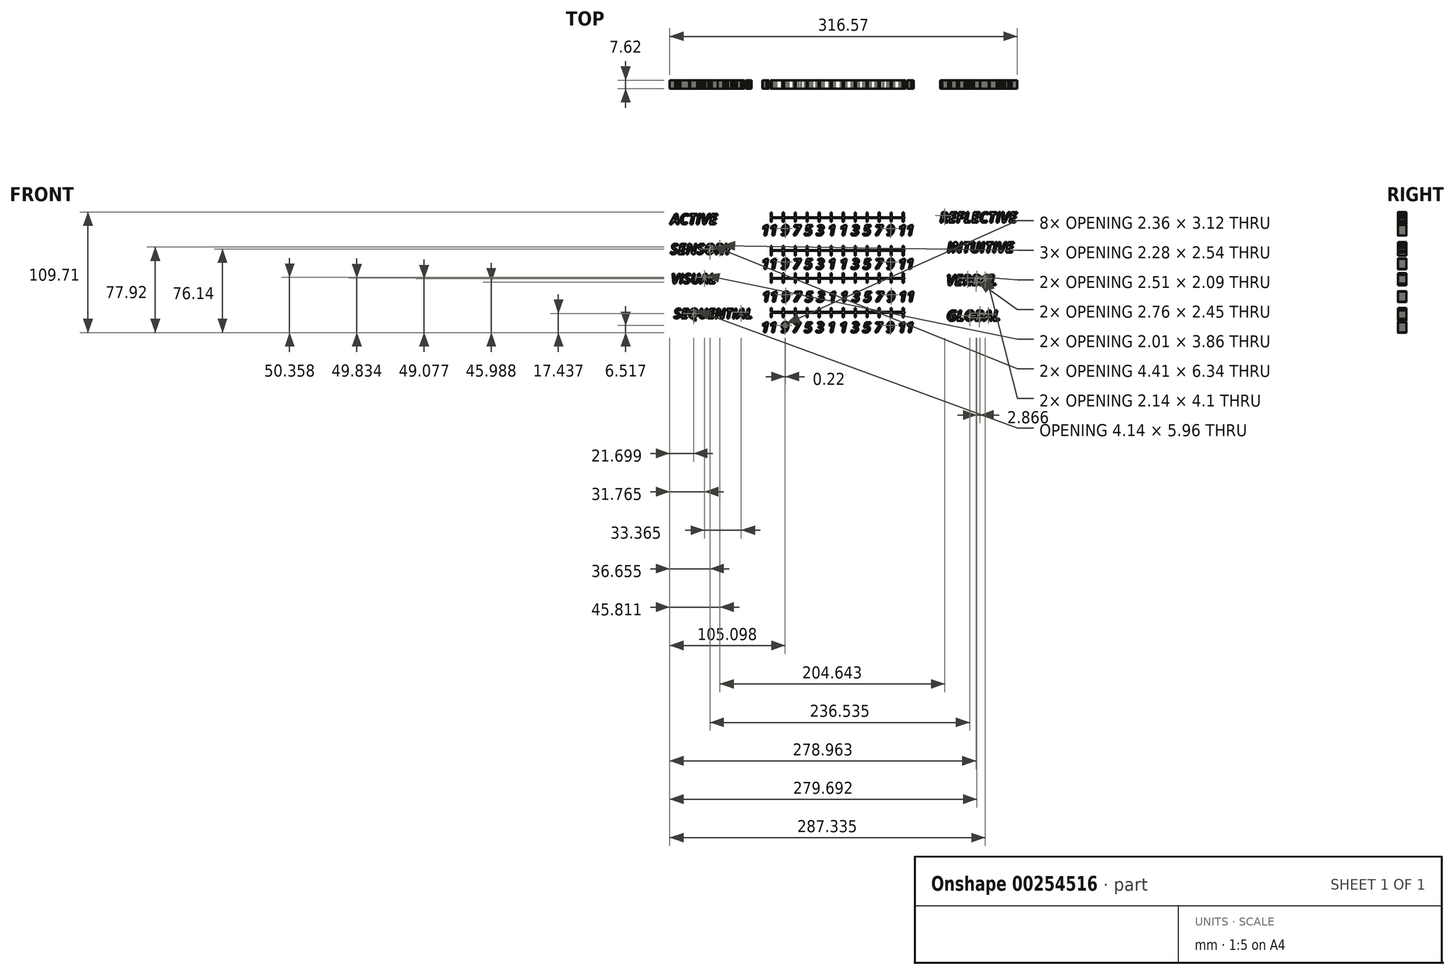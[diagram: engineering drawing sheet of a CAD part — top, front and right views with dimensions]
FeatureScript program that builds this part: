
annotation { "Feature Type Name" : "Feature", "Feature Type Description" : "" }
export const myFeature = defineFeature(function(context is Context, id is Id, definition is map)
    precondition{}
    {
        {
            var Q0;
            Q0=qCreatedBy(makeId("Front.planeOp"),FACE);
            var sketch = newSketch(context, id + "F0", { "sketchPlane" : qUnion([Q0])});
            skText(sketch, "E0", { "text": "ACTIVE", "fontName": "OpenSans-BoldItalic.ttf"});
            skText(sketch, "E1", { "text": "SENSORY", "fontName": "OpenSans-BoldItalic.ttf"});
            skText(sketch, "E2", { "text": "VISUAL", "fontName": "OpenSans-BoldItalic.ttf"});
            skText(sketch, "E3", { "text": "SEQUENTIAL", "fontName": "OpenSans-BoldItalic.ttf"});
            skLineSegment(sketch, "E4", {"start": v(-9.15, 18.36) * mm, "end": v(-99.83, 18.36) * mm});
            skLineSegment(sketch, "E5", {"start": v(-7.58, -9.3) * mm, "end": v(-99.57, -9.3) * mm});
            skLineSegment(sketch, "E6", {"start": v(-99.47, -37.51) * mm, "end": v(-5.07, -37.51) * mm});
            const initialGuessF0  = {"E0": [-0.0995, 0.02725, 1, 0, 0.00948], "E1": [-0.09962, 0, 1, 0, 0.00947], "E2": [-0.09887, -0.02667, 1, 0, 0.0089], "E3": [-0.09653, -0.05842, 1, 0, 0.0089]};
            skSetInitialGuess(sketch, initialGuessF0);
            skSolve(sketch);
        }
        {
            var Q0;
            Q0 = qSketchRegion(id + "F0", true);
            var Q1;
            Q1=qNothing();
            extrude(context, id + "F1", {"entities" : qUnion([Q0, Q1]), "depth" : 7.62 * mm});
        }
        {
            var Q0;
            Q0=qCreatedBy(makeId("Front.planeOp"),FACE);
            var sketch = newSketch(context, id + "F2", { "sketchPlane" : qUnion([Q0])});
            skLineSegment(sketch, "E7.bottom", {"start": v(-101.92, -70.16) * mm, "end": v(120.46, -70.16) * mm});
            skLineSegment(sketch, "E7.top", {"start": v(-101.92, 55.6) * mm, "end": v(120.46, 55.6) * mm});
            skLineSegment(sketch, "E7.left", {"start": v(-101.92, -70.16) * mm, "end": v(-101.92, 55.6) * mm});
            skLineSegment(sketch, "E7.right", {"start": v(120.46, -70.16) * mm, "end": v(120.46, 55.6) * mm});
            skLineSegment(sketch, "E8.bottom", {"start": v(-8.33, 38) * mm, "end": v(-7.22, 38) * mm});
            skLineSegment(sketch, "E8.top", {"start": v(-8.33, 29.27) * mm, "end": v(-7.22, 29.27) * mm});
            skLineSegment(sketch, "E8.left", {"start": v(-8.33, 38) * mm, "end": v(-8.33, 29.27) * mm});
            skLineSegment(sketch, "E8.right", {"start": v(-7.22, 38) * mm, "end": v(-7.22, 29.27) * mm});
            skLineSegment(sketch, "E9.bottom", {"start": v(-8.33, 33.64) * mm, "end": v(113.67, 33.64) * mm});
            skLineSegment(sketch, "E9.top", {"start": v(-8.33, 32.93) * mm, "end": v(113.67, 32.93) * mm});
            skLineSegment(sketch, "E9.left", {"start": v(-8.33, 33.64) * mm, "end": v(-8.33, 32.93) * mm});
            skLineSegment(sketch, "E9.right", {"start": v(113.67, 33.64) * mm, "end": v(113.67, 32.93) * mm});
            skLineSegment(sketch, "E10.1.0.0", {"start": v(2.59, 38) * mm, "end": v(2.59, 29.27) * mm});
            skLineSegment(sketch, "E10.1.0.1", {"start": v(3.7, 38) * mm, "end": v(3.7, 29.27) * mm});
            skLineSegment(sketch, "E10.1.0.2", {"start": v(2.59, 38) * mm, "end": v(3.7, 38) * mm});
            skLineSegment(sketch, "E10.1.0.3", {"start": v(2.59, 29.27) * mm, "end": v(3.7, 29.27) * mm});
            skLineSegment(sketch, "E10.2.0.0", {"start": v(13.51, 38) * mm, "end": v(13.51, 29.27) * mm});
            skLineSegment(sketch, "E10.2.0.1", {"start": v(14.63, 38) * mm, "end": v(14.63, 29.27) * mm});
            skLineSegment(sketch, "E10.2.0.2", {"start": v(13.51, 38) * mm, "end": v(14.63, 38) * mm});
            skLineSegment(sketch, "E10.2.0.3", {"start": v(13.51, 29.27) * mm, "end": v(14.63, 29.27) * mm});
            skLineSegment(sketch, "E10.3.0.0", {"start": v(24.43, 38) * mm, "end": v(24.43, 29.27) * mm});
            skLineSegment(sketch, "E10.3.0.1", {"start": v(25.55, 38) * mm, "end": v(25.55, 29.27) * mm});
            skLineSegment(sketch, "E10.3.0.2", {"start": v(24.43, 38) * mm, "end": v(25.55, 38) * mm});
            skLineSegment(sketch, "E10.3.0.3", {"start": v(24.43, 29.27) * mm, "end": v(25.55, 29.27) * mm});
            skLineSegment(sketch, "E10.4.0.0", {"start": v(35.36, 38) * mm, "end": v(35.36, 29.27) * mm});
            skLineSegment(sketch, "E10.4.0.1", {"start": v(36.47, 38) * mm, "end": v(36.47, 29.27) * mm});
            skLineSegment(sketch, "E10.4.0.2", {"start": v(35.36, 38) * mm, "end": v(36.47, 38) * mm});
            skLineSegment(sketch, "E10.4.0.3", {"start": v(35.36, 29.27) * mm, "end": v(36.47, 29.27) * mm});
            skLineSegment(sketch, "E10.5.0.0", {"start": v(46.28, 38) * mm, "end": v(46.28, 29.27) * mm});
            skLineSegment(sketch, "E10.5.0.1", {"start": v(47.4, 38) * mm, "end": v(47.4, 29.27) * mm});
            skLineSegment(sketch, "E10.5.0.2", {"start": v(46.28, 38) * mm, "end": v(47.4, 38) * mm});
            skLineSegment(sketch, "E10.5.0.3", {"start": v(46.28, 29.27) * mm, "end": v(47.4, 29.27) * mm});
            skLineSegment(sketch, "E10.6.0.0", {"start": v(57.2, 38) * mm, "end": v(57.2, 29.27) * mm});
            skLineSegment(sketch, "E10.6.0.1", {"start": v(58.31, 38) * mm, "end": v(58.31, 29.27) * mm});
            skLineSegment(sketch, "E10.6.0.2", {"start": v(57.2, 38) * mm, "end": v(58.31, 38) * mm});
            skLineSegment(sketch, "E10.6.0.3", {"start": v(57.2, 29.27) * mm, "end": v(58.31, 29.27) * mm});
            skLineSegment(sketch, "E10.7.0.0", {"start": v(68.12, 38) * mm, "end": v(68.12, 29.27) * mm});
            skLineSegment(sketch, "E10.7.0.1", {"start": v(69.24, 38) * mm, "end": v(69.24, 29.27) * mm});
            skLineSegment(sketch, "E10.7.0.2", {"start": v(68.12, 38) * mm, "end": v(69.24, 38) * mm});
            skLineSegment(sketch, "E10.7.0.3", {"start": v(68.12, 29.27) * mm, "end": v(69.24, 29.27) * mm});
            skLineSegment(sketch, "E10.8.0.0", {"start": v(79.04, 38) * mm, "end": v(79.04, 29.27) * mm});
            skLineSegment(sketch, "E10.8.0.1", {"start": v(80.16, 38) * mm, "end": v(80.16, 29.27) * mm});
            skLineSegment(sketch, "E10.8.0.2", {"start": v(79.04, 38) * mm, "end": v(80.16, 38) * mm});
            skLineSegment(sketch, "E10.8.0.3", {"start": v(79.04, 29.27) * mm, "end": v(80.16, 29.27) * mm});
            skLineSegment(sketch, "E10.9.0.0", {"start": v(89.97, 38) * mm, "end": v(89.97, 29.27) * mm});
            skLineSegment(sketch, "E10.9.0.1", {"start": v(91.08, 38) * mm, "end": v(91.08, 29.27) * mm});
            skLineSegment(sketch, "E10.9.0.2", {"start": v(89.97, 38) * mm, "end": v(91.08, 38) * mm});
            skLineSegment(sketch, "E10.9.0.3", {"start": v(89.97, 29.27) * mm, "end": v(91.08, 29.27) * mm});
            skLineSegment(sketch, "E10.10.0.0", {"start": v(100.89, 38) * mm, "end": v(100.89, 29.27) * mm});
            skLineSegment(sketch, "E10.10.0.1", {"start": v(102, 38) * mm, "end": v(102, 29.27) * mm});
            skLineSegment(sketch, "E10.10.0.2", {"start": v(100.89, 38) * mm, "end": v(102, 38) * mm});
            skLineSegment(sketch, "E10.10.0.3", {"start": v(100.89, 29.27) * mm, "end": v(102, 29.27) * mm});
            skLineSegment(sketch, "E10.11.0.0", {"start": v(111.8, 38) * mm, "end": v(111.8, 29.27) * mm});
            skLineSegment(sketch, "E10.11.0.1", {"start": v(112.92, 38) * mm, "end": v(112.92, 29.27) * mm});
            skLineSegment(sketch, "E10.11.0.2", {"start": v(111.8, 38) * mm, "end": v(112.92, 38) * mm});
            skLineSegment(sketch, "E10.11.0.3", {"start": v(111.8, 29.27) * mm, "end": v(112.92, 29.27) * mm});
            skLineSegment(sketch, "E10.direction1", {"start": v(-8.33, 29.27) * mm, "end": v(2.59, 29.27) * mm, "construction": true});
            skLineSegment(sketch, "E11.MirrorCS", {"start": v(2.59, 7.46) * mm, "end": v(3.7, 7.46) * mm});
            skLineSegment(sketch, "E12.MirrorCS", {"start": v(-8.33, 7.46) * mm, "end": v(-7.22, 7.46) * mm});
            skLineSegment(sketch, "E13.MirrorCS", {"start": v(113.67, 3.09) * mm, "end": v(113.67, 3.8) * mm});
            skLineSegment(sketch, "E14.MirrorCS", {"start": v(79.04, 7.46) * mm, "end": v(80.16, 7.46) * mm});
            skLineSegment(sketch, "E15.MirrorCS", {"start": v(111.8, -1.28) * mm, "end": v(112.92, -1.28) * mm});
            skLineSegment(sketch, "E16.MirrorCS", {"start": v(79.04, -1.28) * mm, "end": v(80.16, -1.28) * mm});
            skLineSegment(sketch, "E17.MirrorCS", {"start": v(-8.33, -1.28) * mm, "end": v(-7.22, -1.28) * mm});
            skLineSegment(sketch, "E18.MirrorCS", {"start": v(35.36, 7.46) * mm, "end": v(36.47, 7.46) * mm});
            skLineSegment(sketch, "E19.MirrorCS", {"start": v(13.51, 7.46) * mm, "end": v(14.63, 7.46) * mm});
            skLineSegment(sketch, "E20.MirrorCS", {"start": v(100.89, 7.46) * mm, "end": v(102, 7.46) * mm});
            skLineSegment(sketch, "E21.MirrorCS", {"start": v(-7.22, -1.28) * mm, "end": v(-7.22, 7.46) * mm});
            skLineSegment(sketch, "E22.MirrorCS", {"start": v(24.43, -1.28) * mm, "end": v(25.55, -1.28) * mm});
            skLineSegment(sketch, "E23.MirrorCS", {"start": v(35.36, -1.28) * mm, "end": v(36.47, -1.28) * mm});
            skLineSegment(sketch, "E24.MirrorCS", {"start": v(2.59, -1.28) * mm, "end": v(3.7, -1.28) * mm});
            skLineSegment(sketch, "E25.MirrorCS", {"start": v(111.8, 7.46) * mm, "end": v(112.92, 7.46) * mm});
            skLineSegment(sketch, "E26.MirrorCS", {"start": v(24.43, 7.46) * mm, "end": v(25.55, 7.46) * mm});
            skLineSegment(sketch, "E27.MirrorCS", {"start": v(112.92, -1.28) * mm, "end": v(112.92, 7.46) * mm});
            skLineSegment(sketch, "E28.MirrorCS", {"start": v(89.97, -1.28) * mm, "end": v(91.08, -1.28) * mm});
            skLineSegment(sketch, "E29.MirrorCS", {"start": v(-8.33, 3.09) * mm, "end": v(-8.33, 3.8) * mm});
            skLineSegment(sketch, "E30.MirrorCS", {"start": v(13.51, -1.28) * mm, "end": v(14.63, -1.28) * mm});
            skLineSegment(sketch, "E31.MirrorCS", {"start": v(89.97, 7.46) * mm, "end": v(91.08, 7.46) * mm});
            skLineSegment(sketch, "E32.MirrorCS", {"start": v(68.12, -1.28) * mm, "end": v(69.24, -1.28) * mm});
            skLineSegment(sketch, "E33.MirrorCS", {"start": v(57.2, 7.46) * mm, "end": v(58.31, 7.46) * mm});
            skLineSegment(sketch, "E34.MirrorCS", {"start": v(46.28, 7.46) * mm, "end": v(47.4, 7.46) * mm});
            skLineSegment(sketch, "E35.MirrorCS", {"start": v(68.12, 7.46) * mm, "end": v(69.24, 7.46) * mm});
            skLineSegment(sketch, "E36.MirrorCS", {"start": v(-8.33, -1.28) * mm, "end": v(-8.33, 7.46) * mm});
            skLineSegment(sketch, "E37.MirrorCS", {"start": v(100.89, -1.28) * mm, "end": v(102, -1.28) * mm});
            skLineSegment(sketch, "E38.MirrorCS", {"start": v(111.8, -1.28) * mm, "end": v(111.8, 7.46) * mm});
            skLineSegment(sketch, "E39.MirrorCS", {"start": v(57.2, -1.28) * mm, "end": v(58.31, -1.28) * mm});
            skLineSegment(sketch, "E40.MirrorCS", {"start": v(46.28, -1.28) * mm, "end": v(47.4, -1.28) * mm});
            skLineSegment(sketch, "E41.MirrorCS", {"start": v(-8.33, 3.09) * mm, "end": v(113.67, 3.09) * mm});
            skLineSegment(sketch, "E42.MirrorCS", {"start": v(36.47, -1.28) * mm, "end": v(36.47, 7.46) * mm});
            skLineSegment(sketch, "E43.MirrorCS", {"start": v(35.36, -1.28) * mm, "end": v(35.36, 7.46) * mm});
            skLineSegment(sketch, "E44.MirrorCS", {"start": v(13.51, -1.28) * mm, "end": v(13.51, 7.46) * mm});
            skLineSegment(sketch, "E45.MirrorCS", {"start": v(80.16, -1.28) * mm, "end": v(80.16, 7.46) * mm});
            skLineSegment(sketch, "E46.MirrorCS", {"start": v(69.24, -1.28) * mm, "end": v(69.24, 7.46) * mm});
            skLineSegment(sketch, "E47.MirrorCS", {"start": v(14.63, -1.28) * mm, "end": v(14.63, 7.46) * mm});
            skLineSegment(sketch, "E48.MirrorCS", {"start": v(100.89, -1.28) * mm, "end": v(100.89, 7.46) * mm});
            skLineSegment(sketch, "E49.MirrorCS", {"start": v(25.55, -1.28) * mm, "end": v(25.55, 7.46) * mm});
            skLineSegment(sketch, "E50.MirrorCS", {"start": v(-8.33, 3.8) * mm, "end": v(113.67, 3.8) * mm});
            skLineSegment(sketch, "E51.MirrorCS", {"start": v(91.08, -1.28) * mm, "end": v(91.08, 7.46) * mm});
            skLineSegment(sketch, "E52.MirrorCS", {"start": v(102, -1.28) * mm, "end": v(102, 7.46) * mm});
            skLineSegment(sketch, "E53.MirrorCS", {"start": v(57.2, -1.28) * mm, "end": v(57.2, 7.46) * mm});
            skLineSegment(sketch, "E54.MirrorCS", {"start": v(89.97, -1.28) * mm, "end": v(89.97, 7.46) * mm});
            skLineSegment(sketch, "E55.MirrorCS", {"start": v(-8.33, 7.46) * mm, "end": v(2.59, 7.46) * mm, "construction": true});
            skLineSegment(sketch, "E56.MirrorCS", {"start": v(47.4, -1.28) * mm, "end": v(47.4, 7.46) * mm});
            skLineSegment(sketch, "E57.MirrorCS", {"start": v(68.12, -1.28) * mm, "end": v(68.12, 7.46) * mm});
            skLineSegment(sketch, "E58.MirrorCS", {"start": v(2.59, -1.28) * mm, "end": v(2.59, 7.46) * mm});
            skLineSegment(sketch, "E59.MirrorCS", {"start": v(24.43, -1.28) * mm, "end": v(24.43, 7.46) * mm});
            skLineSegment(sketch, "E60.MirrorCS", {"start": v(3.7, -1.28) * mm, "end": v(3.7, 7.46) * mm});
            skLineSegment(sketch, "E61.MirrorCS", {"start": v(79.04, -1.28) * mm, "end": v(79.04, 7.46) * mm});
            skLineSegment(sketch, "E62.MirrorCS", {"start": v(46.28, -1.28) * mm, "end": v(46.28, 7.46) * mm});
            skLineSegment(sketch, "E63.MirrorCS", {"start": v(58.31, -1.28) * mm, "end": v(58.31, 7.46) * mm});
            skLineSegment(sketch, "E64.MirrorCS", {"start": v(-8.33, -26.06) * mm, "end": v(-7.22, -26.06) * mm});
            skLineSegment(sketch, "E65.MirrorCS", {"start": v(2.59, -26.06) * mm, "end": v(3.7, -26.06) * mm});
            skLineSegment(sketch, "E66.MirrorCS", {"start": v(79.04, -17.33) * mm, "end": v(80.16, -17.33) * mm});
            skLineSegment(sketch, "E67.MirrorCS", {"start": v(-8.33, -17.33) * mm, "end": v(-7.22, -17.33) * mm});
            skLineSegment(sketch, "E68.MirrorCS", {"start": v(57.2, -26.06) * mm, "end": v(58.31, -26.06) * mm});
            skLineSegment(sketch, "E69.MirrorCS", {"start": v(57.2, -17.33) * mm, "end": v(58.31, -17.33) * mm});
            skLineSegment(sketch, "E70.MirrorCS", {"start": v(46.28, -26.06) * mm, "end": v(47.4, -26.06) * mm});
            skLineSegment(sketch, "E71.MirrorCS", {"start": v(35.36, -26.06) * mm, "end": v(36.47, -26.06) * mm});
            skLineSegment(sketch, "E72.MirrorCS", {"start": v(35.36, -17.33) * mm, "end": v(36.47, -17.33) * mm});
            skLineSegment(sketch, "E73.MirrorCS", {"start": v(68.12, -26.06) * mm, "end": v(69.24, -26.06) * mm});
            skLineSegment(sketch, "E74.MirrorCS", {"start": v(13.51, -26.06) * mm, "end": v(14.63, -26.06) * mm});
            skLineSegment(sketch, "E75.MirrorCS", {"start": v(-8.33, -17.33) * mm, "end": v(-8.33, -26.06) * mm});
            skLineSegment(sketch, "E76.MirrorCS", {"start": v(100.89, -26.06) * mm, "end": v(102, -26.06) * mm});
            skLineSegment(sketch, "E77.MirrorCS", {"start": v(46.28, -17.33) * mm, "end": v(47.4, -17.33) * mm});
            skLineSegment(sketch, "E78.MirrorCS", {"start": v(2.59, -17.33) * mm, "end": v(3.7, -17.33) * mm});
            skLineSegment(sketch, "E79.MirrorCS", {"start": v(68.12, -17.33) * mm, "end": v(69.24, -17.33) * mm});
            skLineSegment(sketch, "E80.MirrorCS", {"start": v(13.51, -17.33) * mm, "end": v(14.63, -17.33) * mm});
            skLineSegment(sketch, "E81.MirrorCS", {"start": v(79.04, -26.06) * mm, "end": v(80.16, -26.06) * mm});
            skLineSegment(sketch, "E82.MirrorCS", {"start": v(111.8, -17.33) * mm, "end": v(112.92, -17.33) * mm});
            skLineSegment(sketch, "E83.MirrorCS", {"start": v(89.97, -26.06) * mm, "end": v(91.08, -26.06) * mm});
            skLineSegment(sketch, "E84.MirrorCS", {"start": v(-8.33, -21.7) * mm, "end": v(-8.33, -22.4) * mm});
            skLineSegment(sketch, "E85.MirrorCS", {"start": v(113.67, -21.7) * mm, "end": v(113.67, -22.4) * mm});
            skLineSegment(sketch, "E86.MirrorCS", {"start": v(24.43, -26.06) * mm, "end": v(25.55, -26.06) * mm});
            skLineSegment(sketch, "E87.MirrorCS", {"start": v(24.43, -17.33) * mm, "end": v(25.55, -17.33) * mm});
            skLineSegment(sketch, "E88.MirrorCS", {"start": v(-7.22, -17.33) * mm, "end": v(-7.22, -26.06) * mm});
            skLineSegment(sketch, "E89.MirrorCS", {"start": v(111.8, -17.33) * mm, "end": v(111.8, -26.06) * mm});
            skLineSegment(sketch, "E90.MirrorCS", {"start": v(111.8, -26.06) * mm, "end": v(112.92, -26.06) * mm});
            skLineSegment(sketch, "E91.MirrorCS", {"start": v(112.92, -17.33) * mm, "end": v(112.92, -26.06) * mm});
            skLineSegment(sketch, "E92.MirrorCS", {"start": v(89.97, -17.33) * mm, "end": v(91.08, -17.33) * mm});
            skLineSegment(sketch, "E93.MirrorCS", {"start": v(100.89, -17.33) * mm, "end": v(102, -17.33) * mm});
            skLineSegment(sketch, "E94.MirrorCS", {"start": v(100.89, -17.33) * mm, "end": v(100.89, -26.06) * mm});
            skLineSegment(sketch, "E95.MirrorCS", {"start": v(25.55, -17.33) * mm, "end": v(25.55, -26.06) * mm});
            skLineSegment(sketch, "E96.MirrorCS", {"start": v(-8.33, -26.06) * mm, "end": v(2.59, -26.06) * mm, "construction": true});
            skLineSegment(sketch, "E97.MirrorCS", {"start": v(-8.33, -22.4) * mm, "end": v(113.67, -22.4) * mm});
            skLineSegment(sketch, "E98.MirrorCS", {"start": v(91.08, -17.33) * mm, "end": v(91.08, -26.06) * mm});
            skLineSegment(sketch, "E99.MirrorCS", {"start": v(102, -17.33) * mm, "end": v(102, -26.06) * mm});
            skLineSegment(sketch, "E100.MirrorCS", {"start": v(47.4, -17.33) * mm, "end": v(47.4, -26.06) * mm});
            skLineSegment(sketch, "E101.MirrorCS", {"start": v(69.24, -17.33) * mm, "end": v(69.24, -26.06) * mm});
            skLineSegment(sketch, "E102.MirrorCS", {"start": v(46.28, -17.33) * mm, "end": v(46.28, -26.06) * mm});
            skLineSegment(sketch, "E103.MirrorCS", {"start": v(58.31, -17.33) * mm, "end": v(58.31, -26.06) * mm});
            skLineSegment(sketch, "E104.MirrorCS", {"start": v(14.63, -17.33) * mm, "end": v(14.63, -26.06) * mm});
            skLineSegment(sketch, "E105.MirrorCS", {"start": v(80.16, -17.33) * mm, "end": v(80.16, -26.06) * mm});
            skLineSegment(sketch, "E106.MirrorCS", {"start": v(79.04, -17.33) * mm, "end": v(79.04, -26.06) * mm});
            skLineSegment(sketch, "E107.MirrorCS", {"start": v(68.12, -17.33) * mm, "end": v(68.12, -26.06) * mm});
            skLineSegment(sketch, "E108.MirrorCS", {"start": v(24.43, -17.33) * mm, "end": v(24.43, -26.06) * mm});
            skLineSegment(sketch, "E109.MirrorCS", {"start": v(89.97, -17.33) * mm, "end": v(89.97, -26.06) * mm});
            skLineSegment(sketch, "E110.MirrorCS", {"start": v(13.51, -17.33) * mm, "end": v(13.51, -26.06) * mm});
            skLineSegment(sketch, "E111.MirrorCS", {"start": v(-8.33, -21.7) * mm, "end": v(113.67, -21.7) * mm});
            skLineSegment(sketch, "E112.MirrorCS", {"start": v(2.59, -17.33) * mm, "end": v(2.59, -26.06) * mm});
            skLineSegment(sketch, "E113.MirrorCS", {"start": v(3.7, -17.33) * mm, "end": v(3.7, -26.06) * mm});
            skLineSegment(sketch, "E114.MirrorCS", {"start": v(35.36, -17.33) * mm, "end": v(35.36, -26.06) * mm});
            skLineSegment(sketch, "E115.MirrorCS", {"start": v(36.47, -17.33) * mm, "end": v(36.47, -26.06) * mm});
            skLineSegment(sketch, "E116.MirrorCS", {"start": v(57.2, -17.33) * mm, "end": v(57.2, -26.06) * mm});
            skLineSegment(sketch, "E117.MirrorCS", {"start": v(2.59, -48.96) * mm, "end": v(3.7, -48.96) * mm});
            skLineSegment(sketch, "E118.MirrorCS", {"start": v(-8.33, -53.33) * mm, "end": v(-8.33, -52.62) * mm});
            skLineSegment(sketch, "E119.MirrorCS", {"start": v(-8.33, -48.96) * mm, "end": v(-7.22, -48.96) * mm});
            skLineSegment(sketch, "E120.MirrorCS", {"start": v(89.97, -48.96) * mm, "end": v(91.08, -48.96) * mm});
            skLineSegment(sketch, "E121.MirrorCS", {"start": v(89.97, -57.7) * mm, "end": v(91.08, -57.7) * mm});
            skLineSegment(sketch, "E122.MirrorCS", {"start": v(100.89, -48.96) * mm, "end": v(102, -48.96) * mm});
            skLineSegment(sketch, "E123.MirrorCS", {"start": v(112.92, -57.7) * mm, "end": v(112.92, -48.96) * mm});
            skLineSegment(sketch, "E124.MirrorCS", {"start": v(-8.33, -57.7) * mm, "end": v(-8.33, -48.96) * mm});
            skLineSegment(sketch, "E125.MirrorCS", {"start": v(111.8, -48.96) * mm, "end": v(112.92, -48.96) * mm});
            skLineSegment(sketch, "E126.MirrorCS", {"start": v(13.51, -48.96) * mm, "end": v(14.63, -48.96) * mm});
            skLineSegment(sketch, "E127.MirrorCS", {"start": v(79.04, -57.7) * mm, "end": v(80.16, -57.7) * mm});
            skLineSegment(sketch, "E128.MirrorCS", {"start": v(111.8, -57.7) * mm, "end": v(112.92, -57.7) * mm});
            skLineSegment(sketch, "E129.MirrorCS", {"start": v(68.12, -48.96) * mm, "end": v(69.24, -48.96) * mm});
            skLineSegment(sketch, "E130.MirrorCS", {"start": v(79.04, -48.96) * mm, "end": v(80.16, -48.96) * mm});
            skLineSegment(sketch, "E131.MirrorCS", {"start": v(35.36, -57.7) * mm, "end": v(36.47, -57.7) * mm});
            skLineSegment(sketch, "E132.MirrorCS", {"start": v(-7.22, -57.7) * mm, "end": v(-7.22, -48.96) * mm});
            skLineSegment(sketch, "E133.MirrorCS", {"start": v(46.28, -48.96) * mm, "end": v(47.4, -48.96) * mm});
            skLineSegment(sketch, "E134.MirrorCS", {"start": v(24.43, -48.96) * mm, "end": v(25.55, -48.96) * mm});
            skLineSegment(sketch, "E135.MirrorCS", {"start": v(57.2, -57.7) * mm, "end": v(58.31, -57.7) * mm});
            skLineSegment(sketch, "E136.MirrorCS", {"start": v(113.67, -53.33) * mm, "end": v(113.67, -52.62) * mm});
            skLineSegment(sketch, "E137.MirrorCS", {"start": v(46.28, -57.7) * mm, "end": v(47.4, -57.7) * mm});
            skLineSegment(sketch, "E138.MirrorCS", {"start": v(100.89, -57.7) * mm, "end": v(102, -57.7) * mm});
            skLineSegment(sketch, "E139.MirrorCS", {"start": v(68.12, -57.7) * mm, "end": v(69.24, -57.7) * mm});
            skLineSegment(sketch, "E140.MirrorCS", {"start": v(-8.33, -57.7) * mm, "end": v(-7.22, -57.7) * mm});
            skLineSegment(sketch, "E141.MirrorCS", {"start": v(13.51, -57.7) * mm, "end": v(14.63, -57.7) * mm});
            skLineSegment(sketch, "E142.MirrorCS", {"start": v(57.2, -48.96) * mm, "end": v(58.31, -48.96) * mm});
            skLineSegment(sketch, "E143.MirrorCS", {"start": v(35.36, -48.96) * mm, "end": v(36.47, -48.96) * mm});
            skLineSegment(sketch, "E144.MirrorCS", {"start": v(24.43, -57.7) * mm, "end": v(25.55, -57.7) * mm});
            skLineSegment(sketch, "E145.MirrorCS", {"start": v(2.59, -57.7) * mm, "end": v(3.7, -57.7) * mm});
            skLineSegment(sketch, "E146.MirrorCS", {"start": v(102, -57.7) * mm, "end": v(102, -48.96) * mm});
            skLineSegment(sketch, "E147.MirrorCS", {"start": v(24.43, -57.7) * mm, "end": v(24.43, -48.96) * mm});
            skLineSegment(sketch, "E148.MirrorCS", {"start": v(68.12, -57.7) * mm, "end": v(68.12, -48.96) * mm});
            skLineSegment(sketch, "E149.MirrorCS", {"start": v(79.04, -57.7) * mm, "end": v(79.04, -48.96) * mm});
            skLineSegment(sketch, "E150.MirrorCS", {"start": v(35.36, -57.7) * mm, "end": v(35.36, -48.96) * mm});
            skLineSegment(sketch, "E151.MirrorCS", {"start": v(91.08, -57.7) * mm, "end": v(91.08, -48.96) * mm});
            skLineSegment(sketch, "E152.MirrorCS", {"start": v(111.8, -57.7) * mm, "end": v(111.8, -48.96) * mm});
            skLineSegment(sketch, "E153.MirrorCS", {"start": v(80.16, -57.7) * mm, "end": v(80.16, -48.96) * mm});
            skLineSegment(sketch, "E154.MirrorCS", {"start": v(3.7, -57.7) * mm, "end": v(3.7, -48.96) * mm});
            skLineSegment(sketch, "E155.MirrorCS", {"start": v(14.63, -57.7) * mm, "end": v(14.63, -48.96) * mm});
            skLineSegment(sketch, "E156.MirrorCS", {"start": v(-8.33, -52.62) * mm, "end": v(113.67, -52.62) * mm});
            skLineSegment(sketch, "E157.MirrorCS", {"start": v(46.28, -57.7) * mm, "end": v(46.28, -48.96) * mm});
            skLineSegment(sketch, "E158.MirrorCS", {"start": v(69.24, -57.7) * mm, "end": v(69.24, -48.96) * mm});
            skLineSegment(sketch, "E159.MirrorCS", {"start": v(89.97, -57.7) * mm, "end": v(89.97, -48.96) * mm});
            skLineSegment(sketch, "E160.MirrorCS", {"start": v(25.55, -57.7) * mm, "end": v(25.55, -48.96) * mm});
            skLineSegment(sketch, "E161.MirrorCS", {"start": v(-8.33, -53.33) * mm, "end": v(113.67, -53.33) * mm});
            skLineSegment(sketch, "E162.MirrorCS", {"start": v(13.51, -57.7) * mm, "end": v(13.51, -48.96) * mm});
            skLineSegment(sketch, "E163.MirrorCS", {"start": v(58.31, -57.7) * mm, "end": v(58.31, -48.96) * mm});
            skLineSegment(sketch, "E164.MirrorCS", {"start": v(36.47, -57.7) * mm, "end": v(36.47, -48.96) * mm});
            skLineSegment(sketch, "E165.MirrorCS", {"start": v(57.2, -57.7) * mm, "end": v(57.2, -48.96) * mm});
            skLineSegment(sketch, "E166.MirrorCS", {"start": v(2.59, -57.7) * mm, "end": v(2.59, -48.96) * mm});
            skLineSegment(sketch, "E167.MirrorCS", {"start": v(100.89, -57.7) * mm, "end": v(100.89, -48.96) * mm});
            skLineSegment(sketch, "E168.MirrorCS", {"start": v(47.4, -57.7) * mm, "end": v(47.4, -48.96) * mm});
            skLineSegment(sketch, "E169.MirrorCS", {"start": v(-8.33, -48.96) * mm, "end": v(2.59, -48.96) * mm, "construction": true});
            skSolve(sketch);
        }
        {
            var Q0;
            {var subQ0=sQuery(id+"F2.wireOp",EDGE,"E126.MirrorCS");Q0=makeQuery(id+"F2.imprint","IMPRINT",FACE,{"disambiguationData":[TD([[makeQuery(id+"F2.imprint","IMPRINT",EDGE,{"derivedFrom":subQ0}),-1.0]])]});}
            var Q1;
            {var subQ0=sQuery(id+"F2.wireOp",EDGE,"E142.MirrorCS");Q1=makeQuery(id+"F2.imprint","IMPRINT",FACE,{"disambiguationData":[TD([[makeQuery(id+"F2.imprint","IMPRINT",EDGE,{"derivedFrom":subQ0}),-1.0]])]});}
            var Q2;
            {var subQ0=sQuery(id+"F2.wireOp",EDGE,"E83.MirrorCS");Q2=makeQuery(id+"F2.imprint","IMPRINT",FACE,{"disambiguationData":[TD([[makeQuery(id+"F2.imprint","IMPRINT",EDGE,{"derivedFrom":subQ0}),1.0]])]});}
            var Q3;
            {var subQ0=sQuery(id+"F2.wireOp",EDGE,"E79.MirrorCS");Q3=makeQuery(id+"F2.imprint","IMPRINT",FACE,{"disambiguationData":[TD([[makeQuery(id+"F2.imprint","IMPRINT",EDGE,{"derivedFrom":subQ0}),-1.0]])]});}
            var Q4;
            {var subQ5=sQuery(id+"F2.wireOp",EDGE,"E10.7.0.3");Q4=makeQuery(id+"F2.imprint","IMPRINT",FACE,{"disambiguationData":[TD([[makeQuery(id+"F2.imprint","IMPRINT",EDGE,{"derivedFrom":subQ5}),1.0]])]});}
            var Q5;
            {var subQ0=sQuery(id+"F2.wireOp",EDGE,"E121.MirrorCS");Q5=makeQuery(id+"F2.imprint","IMPRINT",FACE,{"disambiguationData":[TD([[makeQuery(id+"F2.imprint","IMPRINT",EDGE,{"derivedFrom":subQ0}),1.0]])]});}
            var Q6;
            {var subQ5=sQuery(id+"F2.wireOp",EDGE,"E10.6.0.3");Q6=makeQuery(id+"F2.imprint","IMPRINT",FACE,{"disambiguationData":[TD([[makeQuery(id+"F2.imprint","IMPRINT",EDGE,{"derivedFrom":subQ5}),1.0]])]});}
            var Q7;
            {var subQ0=sQuery(id+"F2.wireOp",EDGE,"E19.MirrorCS");Q7=makeQuery(id+"F2.imprint","IMPRINT",FACE,{"disambiguationData":[TD([[makeQuery(id+"F2.imprint","IMPRINT",EDGE,{"derivedFrom":subQ0}),-1.0]])]});}
            var Q8;
            {var subQ0=sQuery(id+"F2.wireOp",EDGE,"E140.MirrorCS");Q8=makeQuery(id+"F2.imprint","IMPRINT",FACE,{"disambiguationData":[TD([[makeQuery(id+"F2.imprint","IMPRINT",EDGE,{"derivedFrom":subQ0}),1.0]])]});}
            var Q9;
            {var subQ0=sQuery(id+"F2.wireOp",EDGE,"E80.MirrorCS");Q9=makeQuery(id+"F2.imprint","IMPRINT",FACE,{"disambiguationData":[TD([[makeQuery(id+"F2.imprint","IMPRINT",EDGE,{"derivedFrom":subQ0}),-1.0]])]});}
            var Q10;
            {var subQ0=sQuery(id+"F2.wireOp",EDGE,"E35.MirrorCS");Q10=makeQuery(id+"F2.imprint","IMPRINT",FACE,{"disambiguationData":[TD([[makeQuery(id+"F2.imprint","IMPRINT",EDGE,{"derivedFrom":subQ0}),-1.0]])]});}
            var Q11;
            {var subQ0=sQuery(id+"F2.wireOp",EDGE,"E39.MirrorCS");Q11=makeQuery(id+"F2.imprint","IMPRINT",FACE,{"disambiguationData":[TD([[makeQuery(id+"F2.imprint","IMPRINT",EDGE,{"derivedFrom":subQ0}),1.0]])]});}
            var Q12;
            {var subQ0=sQuery(id+"F2.wireOp",EDGE,"E22.MirrorCS");Q12=makeQuery(id+"F2.imprint","IMPRINT",FACE,{"disambiguationData":[TD([[makeQuery(id+"F2.imprint","IMPRINT",EDGE,{"derivedFrom":subQ0}),1.0]])]});}
            var Q13;
            {var subQ0=sQuery(id+"F2.wireOp",EDGE,"E139.MirrorCS");Q13=makeQuery(id+"F2.imprint","IMPRINT",FACE,{"disambiguationData":[TD([[makeQuery(id+"F2.imprint","IMPRINT",EDGE,{"derivedFrom":subQ0}),1.0]])]});}
            var Q14;
            {var subQ5=sQuery(id+"F2.wireOp",EDGE,"E10.3.0.3");Q14=makeQuery(id+"F2.imprint","IMPRINT",FACE,{"disambiguationData":[TD([[makeQuery(id+"F2.imprint","IMPRINT",EDGE,{"derivedFrom":subQ5}),1.0]])]});}
            var Q15;
            {var subQ0=sQuery(id+"F2.wireOp",EDGE,"E119.MirrorCS");Q15=makeQuery(id+"F2.imprint","IMPRINT",FACE,{"disambiguationData":[TD([[makeQuery(id+"F2.imprint","IMPRINT",EDGE,{"derivedFrom":subQ0}),-1.0]])]});}
            var Q16;
            {var subQ0=sQuery(id+"F2.wireOp",EDGE,"E33.MirrorCS");Q16=makeQuery(id+"F2.imprint","IMPRINT",FACE,{"disambiguationData":[TD([[makeQuery(id+"F2.imprint","IMPRINT",EDGE,{"derivedFrom":subQ0}),-1.0]])]});}
            var Q17;
            {var subQ0=sQuery(id+"F2.wireOp",EDGE,"E74.MirrorCS");Q17=makeQuery(id+"F2.imprint","IMPRINT",FACE,{"disambiguationData":[TD([[makeQuery(id+"F2.imprint","IMPRINT",EDGE,{"derivedFrom":subQ0}),1.0]])]});}
            var Q18;
            {var subQ0=sQuery(id+"F2.wireOp",EDGE,"E138.MirrorCS");Q18=makeQuery(id+"F2.imprint","IMPRINT",FACE,{"disambiguationData":[TD([[makeQuery(id+"F2.imprint","IMPRINT",EDGE,{"derivedFrom":subQ0}),1.0]])]});}
            var Q19;
            {var subQ0=sQuery(id+"F2.wireOp",EDGE,"E76.MirrorCS");Q19=makeQuery(id+"F2.imprint","IMPRINT",FACE,{"disambiguationData":[TD([[makeQuery(id+"F2.imprint","IMPRINT",EDGE,{"derivedFrom":subQ0}),1.0]])]});}
            var Q20;
            {var subQ0=sQuery(id+"F2.wireOp",EDGE,"E120.MirrorCS");Q20=makeQuery(id+"F2.imprint","IMPRINT",FACE,{"disambiguationData":[TD([[makeQuery(id+"F2.imprint","IMPRINT",EDGE,{"derivedFrom":subQ0}),-1.0]])]});}
            var Q21;
            {var subQ0=sQuery(id+"F2.wireOp",EDGE,"E144.MirrorCS");Q21=makeQuery(id+"F2.imprint","IMPRINT",FACE,{"disambiguationData":[TD([[makeQuery(id+"F2.imprint","IMPRINT",EDGE,{"derivedFrom":subQ0}),1.0]])]});}
            var Q22;
            {var subQ0=sQuery(id+"F2.wireOp",EDGE,"E37.MirrorCS");Q22=makeQuery(id+"F2.imprint","IMPRINT",FACE,{"disambiguationData":[TD([[makeQuery(id+"F2.imprint","IMPRINT",EDGE,{"derivedFrom":subQ0}),1.0]])]});}
            var Q23;
            {var subQ0=sQuery(id+"F2.wireOp",EDGE,"E122.MirrorCS");Q23=makeQuery(id+"F2.imprint","IMPRINT",FACE,{"disambiguationData":[TD([[makeQuery(id+"F2.imprint","IMPRINT",EDGE,{"derivedFrom":subQ0}),-1.0]])]});}
            var Q24;
            {var subQ0=sQuery(id+"F2.wireOp",EDGE,"E141.MirrorCS");Q24=makeQuery(id+"F2.imprint","IMPRINT",FACE,{"disambiguationData":[TD([[makeQuery(id+"F2.imprint","IMPRINT",EDGE,{"derivedFrom":subQ0}),1.0]])]});}
            var Q25;
            {var subQ0=sQuery(id+"F2.wireOp",EDGE,"E17.MirrorCS");Q25=makeQuery(id+"F2.imprint","IMPRINT",FACE,{"disambiguationData":[TD([[makeQuery(id+"F2.imprint","IMPRINT",EDGE,{"derivedFrom":subQ0}),1.0]])]});}
            var Q26;
            {var subQ0=sQuery(id+"F2.wireOp",EDGE,"E20.MirrorCS");Q26=makeQuery(id+"F2.imprint","IMPRINT",FACE,{"disambiguationData":[TD([[makeQuery(id+"F2.imprint","IMPRINT",EDGE,{"derivedFrom":subQ0}),-1.0]])]});}
            var Q27;
            {var subQ0=sQuery(id+"F2.wireOp",EDGE,"E64.MirrorCS");Q27=makeQuery(id+"F2.imprint","IMPRINT",FACE,{"disambiguationData":[TD([[makeQuery(id+"F2.imprint","IMPRINT",EDGE,{"derivedFrom":subQ0}),1.0]])]});}
            var Q28;
            {var subQ0=sQuery(id+"F2.wireOp",EDGE,"E67.MirrorCS");Q28=makeQuery(id+"F2.imprint","IMPRINT",FACE,{"disambiguationData":[TD([[makeQuery(id+"F2.imprint","IMPRINT",EDGE,{"derivedFrom":subQ0}),-1.0]])]});}
            var Q29;
            {var subQ0=sQuery(id+"F2.wireOp",EDGE,"E68.MirrorCS");Q29=makeQuery(id+"F2.imprint","IMPRINT",FACE,{"disambiguationData":[TD([[makeQuery(id+"F2.imprint","IMPRINT",EDGE,{"derivedFrom":subQ0}),1.0]])]});}
            var Q30;
            {var subQ5=sQuery(id+"F2.wireOp",EDGE,"E10.9.0.3");Q30=makeQuery(id+"F2.imprint","IMPRINT",FACE,{"disambiguationData":[TD([[makeQuery(id+"F2.imprint","IMPRINT",EDGE,{"derivedFrom":subQ5}),1.0]])]});}
            var Q31;
            {var subQ0=sQuery(id+"F2.wireOp",EDGE,"E129.MirrorCS");Q31=makeQuery(id+"F2.imprint","IMPRINT",FACE,{"disambiguationData":[TD([[makeQuery(id+"F2.imprint","IMPRINT",EDGE,{"derivedFrom":subQ0}),-1.0]])]});}
            var Q32;
            {var subQ0=sQuery(id+"F2.wireOp",EDGE,"E86.MirrorCS");Q32=makeQuery(id+"F2.imprint","IMPRINT",FACE,{"disambiguationData":[TD([[makeQuery(id+"F2.imprint","IMPRINT",EDGE,{"derivedFrom":subQ0}),1.0]])]});}
            var Q33;
            {var subQ0=sQuery(id+"F2.wireOp",EDGE,"E87.MirrorCS");Q33=makeQuery(id+"F2.imprint","IMPRINT",FACE,{"disambiguationData":[TD([[makeQuery(id+"F2.imprint","IMPRINT",EDGE,{"derivedFrom":subQ0}),-1.0]])]});}
            var Q34;
            {var subQ0=sQuery(id+"F2.wireOp",EDGE,"E69.MirrorCS");Q34=makeQuery(id+"F2.imprint","IMPRINT",FACE,{"disambiguationData":[TD([[makeQuery(id+"F2.imprint","IMPRINT",EDGE,{"derivedFrom":subQ0}),-1.0]])]});}
            var Q35;
            {var subQ0=sQuery(id+"F2.wireOp",EDGE,"E26.MirrorCS");Q35=makeQuery(id+"F2.imprint","IMPRINT",FACE,{"disambiguationData":[TD([[makeQuery(id+"F2.imprint","IMPRINT",EDGE,{"derivedFrom":subQ0}),-1.0]])]});}
            var Q36;
            {var subQ5=sQuery(id+"F2.wireOp",EDGE,"E10.10.0.3");Q36=makeQuery(id+"F2.imprint","IMPRINT",FACE,{"disambiguationData":[TD([[makeQuery(id+"F2.imprint","IMPRINT",EDGE,{"derivedFrom":subQ5}),1.0]])]});}
            var Q37;
            {var subQ0=sQuery(id+"F2.wireOp",EDGE,"E28.MirrorCS");Q37=makeQuery(id+"F2.imprint","IMPRINT",FACE,{"disambiguationData":[TD([[makeQuery(id+"F2.imprint","IMPRINT",EDGE,{"derivedFrom":subQ0}),1.0]])]});}
            var Q38;
            {var subQ0=sQuery(id+"F2.wireOp",EDGE,"E30.MirrorCS");Q38=makeQuery(id+"F2.imprint","IMPRINT",FACE,{"disambiguationData":[TD([[makeQuery(id+"F2.imprint","IMPRINT",EDGE,{"derivedFrom":subQ0}),1.0]])]});}
            var Q39;
            {var subQ0=sQuery(id+"F2.wireOp",EDGE,"E92.MirrorCS");Q39=makeQuery(id+"F2.imprint","IMPRINT",FACE,{"disambiguationData":[TD([[makeQuery(id+"F2.imprint","IMPRINT",EDGE,{"derivedFrom":subQ0}),-1.0]])]});}
            var Q40;
            {var subQ5=sQuery(id+"F2.wireOp",EDGE,"E10.2.0.3");Q40=makeQuery(id+"F2.imprint","IMPRINT",FACE,{"disambiguationData":[TD([[makeQuery(id+"F2.imprint","IMPRINT",EDGE,{"derivedFrom":subQ5}),1.0]])]});}
            var Q41;
            {var subQ0=sQuery(id+"F2.wireOp",EDGE,"E8.bottom");Q41=makeQuery(id+"F2.imprint","IMPRINT",FACE,{"disambiguationData":[TD([[makeQuery(id+"F2.imprint","IMPRINT",EDGE,{"derivedFrom":subQ0}),-1.0]])]});}
            var Q42;
            {var subQ0=sQuery(id+"F2.wireOp",EDGE,"E8.top");Q42=makeQuery(id+"F2.imprint","IMPRINT",FACE,{"disambiguationData":[TD([[makeQuery(id+"F2.imprint","IMPRINT",EDGE,{"derivedFrom":subQ0}),1.0]])]});}
            var Q43;
            {var subQ5=sQuery(id+"F2.wireOp",EDGE,"E10.2.0.2");Q43=makeQuery(id+"F2.imprint","IMPRINT",FACE,{"disambiguationData":[TD([[makeQuery(id+"F2.imprint","IMPRINT",EDGE,{"derivedFrom":subQ5}),-1.0]])]});}
            var Q44;
            {var subQ5=sQuery(id+"F2.wireOp",EDGE,"E10.3.0.2");Q44=makeQuery(id+"F2.imprint","IMPRINT",FACE,{"disambiguationData":[TD([[makeQuery(id+"F2.imprint","IMPRINT",EDGE,{"derivedFrom":subQ5}),-1.0]])]});}
            var Q45;
            {var subQ5=sQuery(id+"F2.wireOp",EDGE,"E10.6.0.2");Q45=makeQuery(id+"F2.imprint","IMPRINT",FACE,{"disambiguationData":[TD([[makeQuery(id+"F2.imprint","IMPRINT",EDGE,{"derivedFrom":subQ5}),-1.0]])]});}
            var Q46;
            {var subQ5=sQuery(id+"F2.wireOp",EDGE,"E10.7.0.2");Q46=makeQuery(id+"F2.imprint","IMPRINT",FACE,{"disambiguationData":[TD([[makeQuery(id+"F2.imprint","IMPRINT",EDGE,{"derivedFrom":subQ5}),-1.0]])]});}
            var Q47;
            {var subQ5=sQuery(id+"F2.wireOp",EDGE,"E10.9.0.2");Q47=makeQuery(id+"F2.imprint","IMPRINT",FACE,{"disambiguationData":[TD([[makeQuery(id+"F2.imprint","IMPRINT",EDGE,{"derivedFrom":subQ5}),-1.0]])]});}
            var Q48;
            {var subQ5=sQuery(id+"F2.wireOp",EDGE,"E10.10.0.2");Q48=makeQuery(id+"F2.imprint","IMPRINT",FACE,{"disambiguationData":[TD([[makeQuery(id+"F2.imprint","IMPRINT",EDGE,{"derivedFrom":subQ5}),-1.0]])]});}
            var Q49;
            {var subQ0=sQuery(id+"F2.wireOp",EDGE,"E31.MirrorCS");Q49=makeQuery(id+"F2.imprint","IMPRINT",FACE,{"disambiguationData":[TD([[makeQuery(id+"F2.imprint","IMPRINT",EDGE,{"derivedFrom":subQ0}),-1.0]])]});}
            var Q50;
            {var subQ0=sQuery(id+"F2.wireOp",EDGE,"E12.MirrorCS");Q50=makeQuery(id+"F2.imprint","IMPRINT",FACE,{"disambiguationData":[TD([[makeQuery(id+"F2.imprint","IMPRINT",EDGE,{"derivedFrom":subQ0}),-1.0]])]});}
            var Q51;
            {var subQ0=sQuery(id+"F2.wireOp",EDGE,"E134.MirrorCS");Q51=makeQuery(id+"F2.imprint","IMPRINT",FACE,{"disambiguationData":[TD([[makeQuery(id+"F2.imprint","IMPRINT",EDGE,{"derivedFrom":subQ0}),-1.0]])]});}
            var Q52;
            {var subQ0=sQuery(id+"F2.wireOp",EDGE,"E93.MirrorCS");Q52=makeQuery(id+"F2.imprint","IMPRINT",FACE,{"disambiguationData":[TD([[makeQuery(id+"F2.imprint","IMPRINT",EDGE,{"derivedFrom":subQ0}),-1.0]])]});}
            var Q53;
            {var subQ0=sQuery(id+"F2.wireOp",EDGE,"E73.MirrorCS");Q53=makeQuery(id+"F2.imprint","IMPRINT",FACE,{"disambiguationData":[TD([[makeQuery(id+"F2.imprint","IMPRINT",EDGE,{"derivedFrom":subQ0}),1.0]])]});}
            var Q54;
            {var subQ0=sQuery(id+"F2.wireOp",EDGE,"E32.MirrorCS");Q54=makeQuery(id+"F2.imprint","IMPRINT",FACE,{"disambiguationData":[TD([[makeQuery(id+"F2.imprint","IMPRINT",EDGE,{"derivedFrom":subQ0}),1.0]])]});}
            var Q55;
            {var subQ0=sQuery(id+"F2.wireOp",EDGE,"E135.MirrorCS");Q55=makeQuery(id+"F2.imprint","IMPRINT",FACE,{"disambiguationData":[TD([[makeQuery(id+"F2.imprint","IMPRINT",EDGE,{"derivedFrom":subQ0}),1.0]])]});}
            var Q56;
            {var subQ0=sQuery(id+"F2.wireOp",EDGE,"E66.MirrorCS");Q56=makeQuery(id+"F2.imprint","IMPRINT",FACE,{"disambiguationData":[TD([[makeQuery(id+"F2.imprint","IMPRINT",EDGE,{"derivedFrom":subQ0}),-1.0]])]});}
            var Q57;
            {var subQ0=sQuery(id+"F2.wireOp",EDGE,"E113.MirrorCS");var subQ1=sQuery(id+"F2.wireOp",EDGE,"E97.MirrorCS");var subQ2=makeQuery(id+"F2.imprint","INTERSECT",VERTEX,{"derivedFrom":[subQ1,subQ0]});Q57=makeQuery(id+"F2.imprint","IMPRINT",FACE,{"disambiguationData":[TD([[makeQuery(id+"F2.imprint","IMPRINT",EDGE,{"disambiguationData":[TD([[subQ2,-1.0]])],"derivedFrom":subQ1}),1.0]])]});}
            var Q58;
            {var subQ0=sQuery(id+"F2.wireOp",EDGE,"E114.MirrorCS");var subQ1=sQuery(id+"F2.wireOp",EDGE,"E97.MirrorCS");var subQ2=makeQuery(id+"F2.imprint","INTERSECT",VERTEX,{"derivedFrom":[subQ1,subQ0]});Q58=makeQuery(id+"F2.imprint","IMPRINT",FACE,{"disambiguationData":[TD([[makeQuery(id+"F2.imprint","IMPRINT",EDGE,{"disambiguationData":[TD([[subQ2,-1.0]])],"derivedFrom":subQ1}),1.0]])]});}
            var Q59;
            {var subQ0=sQuery(id+"F2.wireOp",EDGE,"E115.MirrorCS");var subQ1=sQuery(id+"F2.wireOp",EDGE,"E97.MirrorCS");var subQ2=makeQuery(id+"F2.imprint","INTERSECT",VERTEX,{"derivedFrom":[subQ1,subQ0]});Q59=makeQuery(id+"F2.imprint","IMPRINT",FACE,{"disambiguationData":[TD([[makeQuery(id+"F2.imprint","IMPRINT",EDGE,{"disambiguationData":[TD([[subQ2,-1.0]])],"derivedFrom":subQ1}),1.0]])]});}
            var Q60;
            {var subQ0=sQuery(id+"F2.wireOp",EDGE,"E145.MirrorCS");Q60=makeQuery(id+"F2.imprint","IMPRINT",FACE,{"disambiguationData":[TD([[makeQuery(id+"F2.imprint","IMPRINT",EDGE,{"derivedFrom":subQ0}),1.0]])]});}
            var Q61;
            {var subQ0=sQuery(id+"F2.wireOp",EDGE,"E101.MirrorCS");var subQ1=sQuery(id+"F2.wireOp",EDGE,"E97.MirrorCS");var subQ2=makeQuery(id+"F2.imprint","INTERSECT",VERTEX,{"derivedFrom":[subQ1,subQ0]});Q61=makeQuery(id+"F2.imprint","IMPRINT",FACE,{"disambiguationData":[TD([[makeQuery(id+"F2.imprint","IMPRINT",EDGE,{"disambiguationData":[TD([[subQ2,-1.0]])],"derivedFrom":subQ1}),1.0]])]});}
            var Q62;
            {var subQ0=sQuery(id+"F2.wireOp",EDGE,"E10.10.0.1");var subQ1=sQuery(id+"F2.wireOp",EDGE,"E9.bottom");var subQ2=makeQuery(id+"F2.imprint","INTERSECT",VERTEX,{"derivedFrom":[subQ1,subQ0]});Q62=makeQuery(id+"F2.imprint","IMPRINT",FACE,{"disambiguationData":[TD([[makeQuery(id+"F2.imprint","IMPRINT",EDGE,{"disambiguationData":[TD([[subQ2,-1.0]])],"derivedFrom":subQ1}),-1.0]])]});}
            var Q63;
            {var subQ5=sQuery(id+"F2.wireOp",EDGE,"E10.4.0.3");Q63=makeQuery(id+"F2.imprint","IMPRINT",FACE,{"disambiguationData":[TD([[makeQuery(id+"F2.imprint","IMPRINT",EDGE,{"derivedFrom":subQ5}),1.0]])]});}
            var Q64;
            {var subQ0=sQuery(id+"F2.wireOp",EDGE,"E16.MirrorCS");Q64=makeQuery(id+"F2.imprint","IMPRINT",FACE,{"disambiguationData":[TD([[makeQuery(id+"F2.imprint","IMPRINT",EDGE,{"derivedFrom":subQ0}),1.0]])]});}
            var Q65;
            {var subQ0=sQuery(id+"F2.wireOp",EDGE,"E128.MirrorCS");Q65=makeQuery(id+"F2.imprint","IMPRINT",FACE,{"disambiguationData":[TD([[makeQuery(id+"F2.imprint","IMPRINT",EDGE,{"derivedFrom":subQ0}),1.0]])]});}
            var Q66;
            {var subQ0=sQuery(id+"F2.wireOp",EDGE,"E106.MirrorCS");var subQ1=sQuery(id+"F2.wireOp",EDGE,"E97.MirrorCS");var subQ2=makeQuery(id+"F2.imprint","INTERSECT",VERTEX,{"derivedFrom":[subQ1,subQ0]});Q66=makeQuery(id+"F2.imprint","IMPRINT",FACE,{"disambiguationData":[TD([[makeQuery(id+"F2.imprint","IMPRINT",EDGE,{"disambiguationData":[TD([[subQ2,-1.0]])],"derivedFrom":subQ1}),1.0]])]});}
            var Q67;
            {var subQ0=sQuery(id+"F2.wireOp",EDGE,"E164.MirrorCS");var subQ1=sQuery(id+"F2.wireOp",EDGE,"E156.MirrorCS");var subQ2=makeQuery(id+"F2.imprint","INTERSECT",VERTEX,{"derivedFrom":[subQ1,subQ0]});Q67=makeQuery(id+"F2.imprint","IMPRINT",FACE,{"disambiguationData":[TD([[makeQuery(id+"F2.imprint","IMPRINT",EDGE,{"disambiguationData":[TD([[subQ2,-1.0]])],"derivedFrom":subQ1}),-1.0]])]});}
            var Q68;
            {var subQ0=sQuery(id+"F2.wireOp",EDGE,"E77.MirrorCS");Q68=makeQuery(id+"F2.imprint","IMPRINT",FACE,{"disambiguationData":[TD([[makeQuery(id+"F2.imprint","IMPRINT",EDGE,{"derivedFrom":subQ0}),-1.0]])]});}
            var Q69;
            {var subQ0=sQuery(id+"F2.wireOp",EDGE,"E116.MirrorCS");var subQ1=sQuery(id+"F2.wireOp",EDGE,"E97.MirrorCS");var subQ2=makeQuery(id+"F2.imprint","INTERSECT",VERTEX,{"derivedFrom":[subQ1,subQ0]});Q69=makeQuery(id+"F2.imprint","IMPRINT",FACE,{"disambiguationData":[TD([[makeQuery(id+"F2.imprint","IMPRINT",EDGE,{"disambiguationData":[TD([[subQ2,-1.0]])],"derivedFrom":subQ1}),1.0]])]});}
            var Q70;
            {var subQ0=sQuery(id+"F2.wireOp",EDGE,"E10.3.0.0");var subQ1=sQuery(id+"F2.wireOp",EDGE,"E9.bottom");var subQ2=makeQuery(id+"F2.imprint","INTERSECT",VERTEX,{"derivedFrom":[subQ1,subQ0]});Q70=makeQuery(id+"F2.imprint","IMPRINT",FACE,{"disambiguationData":[TD([[makeQuery(id+"F2.imprint","IMPRINT",EDGE,{"disambiguationData":[TD([[subQ2,-1.0]])],"derivedFrom":subQ1}),-1.0]])]});}
            var Q71;
            {var subQ0=sQuery(id+"F2.wireOp",EDGE,"E82.MirrorCS");Q71=makeQuery(id+"F2.imprint","IMPRINT",FACE,{"disambiguationData":[TD([[makeQuery(id+"F2.imprint","IMPRINT",EDGE,{"derivedFrom":subQ0}),-1.0]])]});}
            var Q72;
            {var subQ0=sQuery(id+"F2.wireOp",EDGE,"E109.MirrorCS");var subQ1=sQuery(id+"F2.wireOp",EDGE,"E97.MirrorCS");var subQ2=makeQuery(id+"F2.imprint","INTERSECT",VERTEX,{"derivedFrom":[subQ1,subQ0]});Q72=makeQuery(id+"F2.imprint","IMPRINT",FACE,{"disambiguationData":[TD([[makeQuery(id+"F2.imprint","IMPRINT",EDGE,{"disambiguationData":[TD([[subQ2,-1.0]])],"derivedFrom":subQ1}),1.0]])]});}
            var Q73;
            {var subQ0=sQuery(id+"F2.wireOp",EDGE,"E18.MirrorCS");Q73=makeQuery(id+"F2.imprint","IMPRINT",FACE,{"disambiguationData":[TD([[makeQuery(id+"F2.imprint","IMPRINT",EDGE,{"derivedFrom":subQ0}),-1.0]])]});}
            var Q74;
            {var subQ0=sQuery(id+"F2.wireOp",EDGE,"E65.MirrorCS");Q74=makeQuery(id+"F2.imprint","IMPRINT",FACE,{"disambiguationData":[TD([[makeQuery(id+"F2.imprint","IMPRINT",EDGE,{"derivedFrom":subQ0}),1.0]])]});}
            var Q75;
            {var subQ0=sQuery(id+"F2.wireOp",EDGE,"E40.MirrorCS");Q75=makeQuery(id+"F2.imprint","IMPRINT",FACE,{"disambiguationData":[TD([[makeQuery(id+"F2.imprint","IMPRINT",EDGE,{"derivedFrom":subQ0}),1.0]])]});}
            var Q76;
            {var subQ0=sQuery(id+"F2.wireOp",EDGE,"E161.MirrorCS");var subQ1=sQuery(id+"F2.wireOp",EDGE,"E153.MirrorCS");var subQ2=makeQuery(id+"F2.imprint","INTERSECT",VERTEX,{"derivedFrom":[subQ1,subQ0]});Q76=makeQuery(id+"F2.imprint","IMPRINT",FACE,{"disambiguationData":[TD([[makeQuery(id+"F2.imprint","IMPRINT",EDGE,{"disambiguationData":[TD([[subQ2,-1.0]])],"derivedFrom":subQ1}),-1.0]])]});}
            var Q77;
            {var subQ0=sQuery(id+"F2.wireOp",EDGE,"E112.MirrorCS");var subQ1=sQuery(id+"F2.wireOp",EDGE,"E97.MirrorCS");var subQ2=makeQuery(id+"F2.imprint","INTERSECT",VERTEX,{"derivedFrom":[subQ1,subQ0]});Q77=makeQuery(id+"F2.imprint","IMPRINT",FACE,{"disambiguationData":[TD([[makeQuery(id+"F2.imprint","IMPRINT",EDGE,{"disambiguationData":[TD([[subQ2,-1.0]])],"derivedFrom":subQ1}),1.0]])]});}
            var Q78;
            {var subQ0=sQuery(id+"F2.wireOp",EDGE,"E161.MirrorCS");var subQ1=sQuery(id+"F2.wireOp",EDGE,"E154.MirrorCS");var subQ2=makeQuery(id+"F2.imprint","INTERSECT",VERTEX,{"derivedFrom":[subQ1,subQ0]});Q78=makeQuery(id+"F2.imprint","IMPRINT",FACE,{"disambiguationData":[TD([[makeQuery(id+"F2.imprint","IMPRINT",EDGE,{"disambiguationData":[TD([[subQ2,-1.0]])],"derivedFrom":subQ1}),1.0]])]});}
            var Q79;
            {var subQ0=sQuery(id+"F2.wireOp",EDGE,"E137.MirrorCS");Q79=makeQuery(id+"F2.imprint","IMPRINT",FACE,{"disambiguationData":[TD([[makeQuery(id+"F2.imprint","IMPRINT",EDGE,{"derivedFrom":subQ0}),1.0]])]});}
            var Q80;
            {var subQ0=sQuery(id+"F2.wireOp",EDGE,"E10.8.0.1");var subQ1=sQuery(id+"F2.wireOp",EDGE,"E9.bottom");var subQ2=makeQuery(id+"F2.imprint","INTERSECT",VERTEX,{"derivedFrom":[subQ1,subQ0]});Q80=makeQuery(id+"F2.imprint","IMPRINT",FACE,{"disambiguationData":[TD([[makeQuery(id+"F2.imprint","IMPRINT",EDGE,{"disambiguationData":[TD([[subQ2,-1.0]])],"derivedFrom":subQ1}),-1.0]])]});}
            var Q81;
            {var subQ0=sQuery(id+"F2.wireOp",EDGE,"E111.MirrorCS");var subQ1=sQuery(id+"F2.wireOp",EDGE,"E94.MirrorCS");var subQ2=makeQuery(id+"F2.imprint","INTERSECT",VERTEX,{"derivedFrom":[subQ1,subQ0]});Q81=makeQuery(id+"F2.imprint","IMPRINT",FACE,{"disambiguationData":[TD([[makeQuery(id+"F2.imprint","IMPRINT",EDGE,{"disambiguationData":[TD([[subQ2,-1.0]])],"derivedFrom":subQ1}),-1.0]])]});}
            var Q82;
            {var subQ0=sQuery(id+"F2.wireOp",EDGE,"E14.MirrorCS");Q82=makeQuery(id+"F2.imprint","IMPRINT",FACE,{"disambiguationData":[TD([[makeQuery(id+"F2.imprint","IMPRINT",EDGE,{"derivedFrom":subQ0}),-1.0]])]});}
            var Q83;
            {var subQ0=sQuery(id+"F2.wireOp",EDGE,"E23.MirrorCS");Q83=makeQuery(id+"F2.imprint","IMPRINT",FACE,{"disambiguationData":[TD([[makeQuery(id+"F2.imprint","IMPRINT",EDGE,{"derivedFrom":subQ0}),1.0]])]});}
            var Q84;
            {var subQ0=sQuery(id+"F2.wireOp",EDGE,"E10.4.0.0");var subQ1=sQuery(id+"F2.wireOp",EDGE,"E9.bottom");var subQ2=makeQuery(id+"F2.imprint","INTERSECT",VERTEX,{"derivedFrom":[subQ1,subQ0]});Q84=makeQuery(id+"F2.imprint","IMPRINT",FACE,{"disambiguationData":[TD([[makeQuery(id+"F2.imprint","IMPRINT",EDGE,{"disambiguationData":[TD([[subQ2,-1.0]])],"derivedFrom":subQ1}),-1.0]])]});}
            var Q85;
            {var subQ0=sQuery(id+"F2.wireOp",EDGE,"E105.MirrorCS");var subQ1=sQuery(id+"F2.wireOp",EDGE,"E97.MirrorCS");var subQ2=makeQuery(id+"F2.imprint","INTERSECT",VERTEX,{"derivedFrom":[subQ1,subQ0]});Q85=makeQuery(id+"F2.imprint","IMPRINT",FACE,{"disambiguationData":[TD([[makeQuery(id+"F2.imprint","IMPRINT",EDGE,{"disambiguationData":[TD([[subQ2,-1.0]])],"derivedFrom":subQ1}),1.0]])]});}
            var Q86;
            {var subQ0=sQuery(id+"F2.wireOp",EDGE,"E9.bottom");var subQ1=sQuery(id+"F2.wireOp",EDGE,"E8.right");var subQ2=makeQuery(id+"F2.imprint","INTERSECT",VERTEX,{"derivedFrom":[subQ1,subQ0]});Q86=makeQuery(id+"F2.imprint","IMPRINT",FACE,{"disambiguationData":[TD([[makeQuery(id+"F2.imprint","IMPRINT",EDGE,{"disambiguationData":[TD([[subQ2,-1.0]])],"derivedFrom":subQ1}),1.0]])]});}
            var Q87;
            {var subQ0=sQuery(id+"F2.wireOp",EDGE,"E110.MirrorCS");var subQ1=sQuery(id+"F2.wireOp",EDGE,"E97.MirrorCS");var subQ2=makeQuery(id+"F2.imprint","INTERSECT",VERTEX,{"derivedFrom":[subQ1,subQ0]});Q87=makeQuery(id+"F2.imprint","IMPRINT",FACE,{"disambiguationData":[TD([[makeQuery(id+"F2.imprint","IMPRINT",EDGE,{"disambiguationData":[TD([[subQ2,-1.0]])],"derivedFrom":subQ1}),1.0]])]});}
            var Q88;
            {var subQ0=sQuery(id+"F2.wireOp",EDGE,"E161.MirrorCS");var subQ1=sQuery(id+"F2.wireOp",EDGE,"E155.MirrorCS");var subQ2=makeQuery(id+"F2.imprint","INTERSECT",VERTEX,{"derivedFrom":[subQ1,subQ0]});Q88=makeQuery(id+"F2.imprint","IMPRINT",FACE,{"disambiguationData":[TD([[makeQuery(id+"F2.imprint","IMPRINT",EDGE,{"disambiguationData":[TD([[subQ2,-1.0]])],"derivedFrom":subQ1}),1.0]])]});}
            var Q89;
            {var subQ0=sQuery(id+"F2.wireOp",EDGE,"E10.9.0.1");var subQ1=sQuery(id+"F2.wireOp",EDGE,"E9.bottom");var subQ2=makeQuery(id+"F2.imprint","INTERSECT",VERTEX,{"derivedFrom":[subQ1,subQ0]});Q89=makeQuery(id+"F2.imprint","IMPRINT",FACE,{"disambiguationData":[TD([[makeQuery(id+"F2.imprint","IMPRINT",EDGE,{"disambiguationData":[TD([[subQ2,-1.0]])],"derivedFrom":subQ1}),-1.0]])]});}
            var Q90;
            {var subQ0=sQuery(id+"F2.wireOp",EDGE,"E111.MirrorCS");var subQ1=sQuery(id+"F2.wireOp",EDGE,"E95.MirrorCS");var subQ2=makeQuery(id+"F2.imprint","INTERSECT",VERTEX,{"derivedFrom":[subQ1,subQ0]});Q90=makeQuery(id+"F2.imprint","IMPRINT",FACE,{"disambiguationData":[TD([[makeQuery(id+"F2.imprint","IMPRINT",EDGE,{"disambiguationData":[TD([[subQ2,-1.0]])],"derivedFrom":subQ1}),1.0]])]});}
            var Q91;
            {var subQ0=sQuery(id+"F2.wireOp",EDGE,"E161.MirrorCS");var subQ1=sQuery(id+"F2.wireOp",EDGE,"E154.MirrorCS");var subQ2=makeQuery(id+"F2.imprint","INTERSECT",VERTEX,{"derivedFrom":[subQ1,subQ0]});Q91=makeQuery(id+"F2.imprint","IMPRINT",FACE,{"disambiguationData":[TD([[makeQuery(id+"F2.imprint","IMPRINT",EDGE,{"disambiguationData":[TD([[subQ2,-1.0]])],"derivedFrom":subQ1}),-1.0]])]});}
            var Q92;
            {var subQ0=sQuery(id+"F2.wireOp",EDGE,"E15.MirrorCS");Q92=makeQuery(id+"F2.imprint","IMPRINT",FACE,{"disambiguationData":[TD([[makeQuery(id+"F2.imprint","IMPRINT",EDGE,{"derivedFrom":subQ0}),1.0]])]});}
            var Q93;
            {var subQ0=sQuery(id+"F2.wireOp",EDGE,"E34.MirrorCS");Q93=makeQuery(id+"F2.imprint","IMPRINT",FACE,{"disambiguationData":[TD([[makeQuery(id+"F2.imprint","IMPRINT",EDGE,{"derivedFrom":subQ0}),-1.0]])]});}
            var Q94;
            {var subQ0=sQuery(id+"F2.wireOp",EDGE,"E103.MirrorCS");var subQ1=sQuery(id+"F2.wireOp",EDGE,"E97.MirrorCS");var subQ2=makeQuery(id+"F2.imprint","INTERSECT",VERTEX,{"derivedFrom":[subQ1,subQ0]});Q94=makeQuery(id+"F2.imprint","IMPRINT",FACE,{"disambiguationData":[TD([[makeQuery(id+"F2.imprint","IMPRINT",EDGE,{"disambiguationData":[TD([[subQ2,-1.0]])],"derivedFrom":subQ1}),1.0]])]});}
            var Q95;
            {var subQ0=sQuery(id+"F2.wireOp",EDGE,"E104.MirrorCS");var subQ1=sQuery(id+"F2.wireOp",EDGE,"E97.MirrorCS");var subQ2=makeQuery(id+"F2.imprint","INTERSECT",VERTEX,{"derivedFrom":[subQ1,subQ0]});Q95=makeQuery(id+"F2.imprint","IMPRINT",FACE,{"disambiguationData":[TD([[makeQuery(id+"F2.imprint","IMPRINT",EDGE,{"disambiguationData":[TD([[subQ2,-1.0]])],"derivedFrom":subQ1}),1.0]])]});}
            var Q96;
            {var subQ0=sQuery(id+"F2.wireOp",EDGE,"E168.MirrorCS");var subQ1=sQuery(id+"F2.wireOp",EDGE,"E156.MirrorCS");var subQ2=makeQuery(id+"F2.imprint","INTERSECT",VERTEX,{"derivedFrom":[subQ1,subQ0]});Q96=makeQuery(id+"F2.imprint","IMPRINT",FACE,{"disambiguationData":[TD([[makeQuery(id+"F2.imprint","IMPRINT",EDGE,{"disambiguationData":[TD([[subQ2,-1.0]])],"derivedFrom":subQ1}),-1.0]])]});}
            var Q97;
            {var subQ0=sQuery(id+"F2.wireOp",EDGE,"E78.MirrorCS");Q97=makeQuery(id+"F2.imprint","IMPRINT",FACE,{"disambiguationData":[TD([[makeQuery(id+"F2.imprint","IMPRINT",EDGE,{"derivedFrom":subQ0}),-1.0]])]});}
            var Q98;
            {var subQ0=sQuery(id+"F2.wireOp",EDGE,"E102.MirrorCS");var subQ1=sQuery(id+"F2.wireOp",EDGE,"E97.MirrorCS");var subQ2=makeQuery(id+"F2.imprint","INTERSECT",VERTEX,{"derivedFrom":[subQ1,subQ0]});Q98=makeQuery(id+"F2.imprint","IMPRINT",FACE,{"disambiguationData":[TD([[makeQuery(id+"F2.imprint","IMPRINT",EDGE,{"disambiguationData":[TD([[subQ2,-1.0]])],"derivedFrom":subQ1}),1.0]])]});}
            var Q99;
            {var subQ0=sQuery(id+"F2.wireOp",EDGE,"E10.2.0.0");var subQ1=sQuery(id+"F2.wireOp",EDGE,"E9.bottom");var subQ2=makeQuery(id+"F2.imprint","INTERSECT",VERTEX,{"derivedFrom":[subQ1,subQ0]});Q99=makeQuery(id+"F2.imprint","IMPRINT",FACE,{"disambiguationData":[TD([[makeQuery(id+"F2.imprint","IMPRINT",EDGE,{"disambiguationData":[TD([[subQ2,-1.0]])],"derivedFrom":subQ1}),-1.0]])]});}
            var Q100;
            {var subQ0=sQuery(id+"F2.wireOp",EDGE,"E81.MirrorCS");Q100=makeQuery(id+"F2.imprint","IMPRINT",FACE,{"disambiguationData":[TD([[makeQuery(id+"F2.imprint","IMPRINT",EDGE,{"derivedFrom":subQ0}),1.0]])]});}
            var Q101;
            {var subQ0=sQuery(id+"F2.wireOp",EDGE,"E125.MirrorCS");Q101=makeQuery(id+"F2.imprint","IMPRINT",FACE,{"disambiguationData":[TD([[makeQuery(id+"F2.imprint","IMPRINT",EDGE,{"derivedFrom":subQ0}),-1.0]])]});}
            var Q102;
            {var subQ5=sQuery(id+"F2.wireOp",EDGE,"E10.5.0.3");Q102=makeQuery(id+"F2.imprint","IMPRINT",FACE,{"disambiguationData":[TD([[makeQuery(id+"F2.imprint","IMPRINT",EDGE,{"derivedFrom":subQ5}),1.0]])]});}
            var Q103;
            {var subQ0=sQuery(id+"F2.wireOp",EDGE,"E165.MirrorCS");var subQ1=sQuery(id+"F2.wireOp",EDGE,"E156.MirrorCS");var subQ2=makeQuery(id+"F2.imprint","INTERSECT",VERTEX,{"derivedFrom":[subQ1,subQ0]});Q103=makeQuery(id+"F2.imprint","IMPRINT",FACE,{"disambiguationData":[TD([[makeQuery(id+"F2.imprint","IMPRINT",EDGE,{"disambiguationData":[TD([[subQ2,-1.0]])],"derivedFrom":subQ1}),-1.0]])]});}
            var Q104;
            {var subQ0=sQuery(id+"F2.wireOp",EDGE,"E107.MirrorCS");var subQ1=sQuery(id+"F2.wireOp",EDGE,"E97.MirrorCS");var subQ2=makeQuery(id+"F2.imprint","INTERSECT",VERTEX,{"derivedFrom":[subQ1,subQ0]});Q104=makeQuery(id+"F2.imprint","IMPRINT",FACE,{"disambiguationData":[TD([[makeQuery(id+"F2.imprint","IMPRINT",EDGE,{"disambiguationData":[TD([[subQ2,-1.0]])],"derivedFrom":subQ1}),1.0]])]});}
            var Q105;
            {var subQ0=sQuery(id+"F2.wireOp",EDGE,"E143.MirrorCS");Q105=makeQuery(id+"F2.imprint","IMPRINT",FACE,{"disambiguationData":[TD([[makeQuery(id+"F2.imprint","IMPRINT",EDGE,{"derivedFrom":subQ0}),-1.0]])]});}
            var Q106;
            {var subQ0=sQuery(id+"F2.wireOp",EDGE,"E100.MirrorCS");var subQ1=sQuery(id+"F2.wireOp",EDGE,"E97.MirrorCS");var subQ2=makeQuery(id+"F2.imprint","INTERSECT",VERTEX,{"derivedFrom":[subQ1,subQ0]});Q106=makeQuery(id+"F2.imprint","IMPRINT",FACE,{"disambiguationData":[TD([[makeQuery(id+"F2.imprint","IMPRINT",EDGE,{"disambiguationData":[TD([[subQ2,-1.0]])],"derivedFrom":subQ1}),1.0]])]});}
            var Q107;
            {var subQ0=sQuery(id+"F2.wireOp",EDGE,"E10.1.0.0");var subQ1=sQuery(id+"F2.wireOp",EDGE,"E9.bottom");var subQ2=makeQuery(id+"F2.imprint","INTERSECT",VERTEX,{"derivedFrom":[subQ1,subQ0]});Q107=makeQuery(id+"F2.imprint","IMPRINT",FACE,{"disambiguationData":[TD([[makeQuery(id+"F2.imprint","IMPRINT",EDGE,{"disambiguationData":[TD([[subQ2,-1.0]])],"derivedFrom":subQ1}),-1.0]])]});}
            var Q108;
            {var subQ5=sQuery(id+"F2.wireOp",EDGE,"E10.8.0.3");Q108=makeQuery(id+"F2.imprint","IMPRINT",FACE,{"disambiguationData":[TD([[makeQuery(id+"F2.imprint","IMPRINT",EDGE,{"derivedFrom":subQ5}),1.0]])]});}
            var Q109;
            {var subQ0=sQuery(id+"F2.wireOp",EDGE,"E127.MirrorCS");Q109=makeQuery(id+"F2.imprint","IMPRINT",FACE,{"disambiguationData":[TD([[makeQuery(id+"F2.imprint","IMPRINT",EDGE,{"derivedFrom":subQ0}),1.0]])]});}
            var Q110;
            {var subQ0=sQuery(id+"F2.wireOp",EDGE,"E24.MirrorCS");Q110=makeQuery(id+"F2.imprint","IMPRINT",FACE,{"disambiguationData":[TD([[makeQuery(id+"F2.imprint","IMPRINT",EDGE,{"derivedFrom":subQ0}),1.0]])]});}
            var Q111;
            {var subQ0=sQuery(id+"F2.wireOp",EDGE,"E10.5.0.0");var subQ1=sQuery(id+"F2.wireOp",EDGE,"E9.bottom");var subQ2=makeQuery(id+"F2.imprint","INTERSECT",VERTEX,{"derivedFrom":[subQ1,subQ0]});Q111=makeQuery(id+"F2.imprint","IMPRINT",FACE,{"disambiguationData":[TD([[makeQuery(id+"F2.imprint","IMPRINT",EDGE,{"disambiguationData":[TD([[subQ2,-1.0]])],"derivedFrom":subQ1}),-1.0]])]});}
            var Q112;
            {var subQ0=sQuery(id+"F2.wireOp",EDGE,"E161.MirrorCS");var subQ1=sQuery(id+"F2.wireOp",EDGE,"E132.MirrorCS");var subQ2=makeQuery(id+"F2.imprint","INTERSECT",VERTEX,{"derivedFrom":[subQ1,subQ0]});Q112=makeQuery(id+"F2.imprint","IMPRINT",FACE,{"disambiguationData":[TD([[makeQuery(id+"F2.imprint","IMPRINT",EDGE,{"disambiguationData":[TD([[subQ2,-1.0]])],"derivedFrom":subQ1}),-1.0]])]});}
            var Q113;
            {var subQ0=sQuery(id+"F2.wireOp",EDGE,"E10.1.0.1");var subQ1=sQuery(id+"F2.wireOp",EDGE,"E9.bottom");var subQ2=makeQuery(id+"F2.imprint","INTERSECT",VERTEX,{"derivedFrom":[subQ1,subQ0]});Q113=makeQuery(id+"F2.imprint","IMPRINT",FACE,{"disambiguationData":[TD([[makeQuery(id+"F2.imprint","IMPRINT",EDGE,{"disambiguationData":[TD([[subQ2,-1.0]])],"derivedFrom":subQ1}),-1.0]])]});}
            var Q114;
            {var subQ0=sQuery(id+"F2.wireOp",EDGE,"E25.MirrorCS");Q114=makeQuery(id+"F2.imprint","IMPRINT",FACE,{"disambiguationData":[TD([[makeQuery(id+"F2.imprint","IMPRINT",EDGE,{"derivedFrom":subQ0}),-1.0]])]});}
            var Q115;
            {var subQ0=sQuery(id+"F2.wireOp",EDGE,"E10.2.0.1");var subQ1=sQuery(id+"F2.wireOp",EDGE,"E9.bottom");var subQ2=makeQuery(id+"F2.imprint","INTERSECT",VERTEX,{"derivedFrom":[subQ1,subQ0]});Q115=makeQuery(id+"F2.imprint","IMPRINT",FACE,{"disambiguationData":[TD([[makeQuery(id+"F2.imprint","IMPRINT",EDGE,{"disambiguationData":[TD([[subQ2,-1.0]])],"derivedFrom":subQ1}),-1.0]])]});}
            var Q116;
            {var subQ0=sQuery(id+"F2.wireOp",EDGE,"E161.MirrorCS");var subQ1=sQuery(id+"F2.wireOp",EDGE,"E146.MirrorCS");var subQ2=makeQuery(id+"F2.imprint","INTERSECT",VERTEX,{"derivedFrom":[subQ1,subQ0]});Q116=makeQuery(id+"F2.imprint","IMPRINT",FACE,{"disambiguationData":[TD([[makeQuery(id+"F2.imprint","IMPRINT",EDGE,{"disambiguationData":[TD([[subQ2,-1.0]])],"derivedFrom":subQ1}),1.0]])]});}
            var Q117;
            {var subQ0=sQuery(id+"F2.wireOp",EDGE,"E10.6.0.0");var subQ1=sQuery(id+"F2.wireOp",EDGE,"E9.bottom");var subQ2=makeQuery(id+"F2.imprint","INTERSECT",VERTEX,{"derivedFrom":[subQ1,subQ0]});Q117=makeQuery(id+"F2.imprint","IMPRINT",FACE,{"disambiguationData":[TD([[makeQuery(id+"F2.imprint","IMPRINT",EDGE,{"disambiguationData":[TD([[subQ2,-1.0]])],"derivedFrom":subQ1}),-1.0]])]});}
            var Q118;
            {var subQ0=sQuery(id+"F2.wireOp",EDGE,"E161.MirrorCS");var subQ1=sQuery(id+"F2.wireOp",EDGE,"E146.MirrorCS");var subQ2=makeQuery(id+"F2.imprint","INTERSECT",VERTEX,{"derivedFrom":[subQ1,subQ0]});Q118=makeQuery(id+"F2.imprint","IMPRINT",FACE,{"disambiguationData":[TD([[makeQuery(id+"F2.imprint","IMPRINT",EDGE,{"disambiguationData":[TD([[subQ2,-1.0]])],"derivedFrom":subQ1}),-1.0]])]});}
            var Q119;
            {var subQ0=sQuery(id+"F2.wireOp",EDGE,"E10.3.0.1");var subQ1=sQuery(id+"F2.wireOp",EDGE,"E9.bottom");var subQ2=makeQuery(id+"F2.imprint","INTERSECT",VERTEX,{"derivedFrom":[subQ1,subQ0]});Q119=makeQuery(id+"F2.imprint","IMPRINT",FACE,{"disambiguationData":[TD([[makeQuery(id+"F2.imprint","IMPRINT",EDGE,{"disambiguationData":[TD([[subQ2,-1.0]])],"derivedFrom":subQ1}),-1.0]])]});}
            var Q120;
            {var subQ0=sQuery(id+"F2.wireOp",EDGE,"E130.MirrorCS");Q120=makeQuery(id+"F2.imprint","IMPRINT",FACE,{"disambiguationData":[TD([[makeQuery(id+"F2.imprint","IMPRINT",EDGE,{"derivedFrom":subQ0}),-1.0]])]});}
            var Q121;
            {var subQ0=sQuery(id+"F2.wireOp",EDGE,"E161.MirrorCS");var subQ1=sQuery(id+"F2.wireOp",EDGE,"E147.MirrorCS");var subQ2=makeQuery(id+"F2.imprint","INTERSECT",VERTEX,{"derivedFrom":[subQ1,subQ0]});Q121=makeQuery(id+"F2.imprint","IMPRINT",FACE,{"disambiguationData":[TD([[makeQuery(id+"F2.imprint","IMPRINT",EDGE,{"disambiguationData":[TD([[subQ2,-1.0]])],"derivedFrom":subQ1}),-1.0]])]});}
            var Q122;
            {var subQ0=sQuery(id+"F2.wireOp",EDGE,"E10.7.0.0");var subQ1=sQuery(id+"F2.wireOp",EDGE,"E9.bottom");var subQ2=makeQuery(id+"F2.imprint","INTERSECT",VERTEX,{"derivedFrom":[subQ1,subQ0]});Q122=makeQuery(id+"F2.imprint","IMPRINT",FACE,{"disambiguationData":[TD([[makeQuery(id+"F2.imprint","IMPRINT",EDGE,{"disambiguationData":[TD([[subQ2,-1.0]])],"derivedFrom":subQ1}),-1.0]])]});}
            var Q123;
            {var subQ0=sQuery(id+"F2.wireOp",EDGE,"E161.MirrorCS");var subQ1=sQuery(id+"F2.wireOp",EDGE,"E147.MirrorCS");var subQ2=makeQuery(id+"F2.imprint","INTERSECT",VERTEX,{"derivedFrom":[subQ1,subQ0]});Q123=makeQuery(id+"F2.imprint","IMPRINT",FACE,{"disambiguationData":[TD([[makeQuery(id+"F2.imprint","IMPRINT",EDGE,{"disambiguationData":[TD([[subQ2,-1.0]])],"derivedFrom":subQ1}),1.0]])]});}
            var Q124;
            {var subQ0=sQuery(id+"F2.wireOp",EDGE,"E161.MirrorCS");var subQ1=sQuery(id+"F2.wireOp",EDGE,"E148.MirrorCS");var subQ2=makeQuery(id+"F2.imprint","INTERSECT",VERTEX,{"derivedFrom":[subQ1,subQ0]});Q124=makeQuery(id+"F2.imprint","IMPRINT",FACE,{"disambiguationData":[TD([[makeQuery(id+"F2.imprint","IMPRINT",EDGE,{"disambiguationData":[TD([[subQ2,-1.0]])],"derivedFrom":subQ1}),-1.0]])]});}
            var Q125;
            {var subQ0=sQuery(id+"F2.wireOp",EDGE,"E10.8.0.0");var subQ1=sQuery(id+"F2.wireOp",EDGE,"E9.bottom");var subQ2=makeQuery(id+"F2.imprint","INTERSECT",VERTEX,{"derivedFrom":[subQ1,subQ0]});Q125=makeQuery(id+"F2.imprint","IMPRINT",FACE,{"disambiguationData":[TD([[makeQuery(id+"F2.imprint","IMPRINT",EDGE,{"disambiguationData":[TD([[subQ2,-1.0]])],"derivedFrom":subQ1}),-1.0]])]});}
            var Q126;
            {var subQ0=sQuery(id+"F2.wireOp",EDGE,"E161.MirrorCS");var subQ1=sQuery(id+"F2.wireOp",EDGE,"E148.MirrorCS");var subQ2=makeQuery(id+"F2.imprint","INTERSECT",VERTEX,{"derivedFrom":[subQ1,subQ0]});Q126=makeQuery(id+"F2.imprint","IMPRINT",FACE,{"disambiguationData":[TD([[makeQuery(id+"F2.imprint","IMPRINT",EDGE,{"disambiguationData":[TD([[subQ2,-1.0]])],"derivedFrom":subQ1}),1.0]])]});}
            var Q127;
            {var subQ0=sQuery(id+"F2.wireOp",EDGE,"E70.MirrorCS");Q127=makeQuery(id+"F2.imprint","IMPRINT",FACE,{"disambiguationData":[TD([[makeQuery(id+"F2.imprint","IMPRINT",EDGE,{"derivedFrom":subQ0}),1.0]])]});}
            var Q128;
            {var subQ5=sQuery(id+"F2.wireOp",EDGE,"E10.11.0.3");Q128=makeQuery(id+"F2.imprint","IMPRINT",FACE,{"disambiguationData":[TD([[makeQuery(id+"F2.imprint","IMPRINT",EDGE,{"derivedFrom":subQ5}),1.0]])]});}
            var Q129;
            {var subQ0=sQuery(id+"F2.wireOp",EDGE,"E10.4.0.1");var subQ1=sQuery(id+"F2.wireOp",EDGE,"E9.bottom");var subQ2=makeQuery(id+"F2.imprint","INTERSECT",VERTEX,{"derivedFrom":[subQ1,subQ0]});Q129=makeQuery(id+"F2.imprint","IMPRINT",FACE,{"disambiguationData":[TD([[makeQuery(id+"F2.imprint","IMPRINT",EDGE,{"disambiguationData":[TD([[subQ2,-1.0]])],"derivedFrom":subQ1}),-1.0]])]});}
            var Q130;
            {var subQ0=sQuery(id+"F2.wireOp",EDGE,"E131.MirrorCS");Q130=makeQuery(id+"F2.imprint","IMPRINT",FACE,{"disambiguationData":[TD([[makeQuery(id+"F2.imprint","IMPRINT",EDGE,{"derivedFrom":subQ0}),1.0]])]});}
            var Q131;
            {var subQ0=sQuery(id+"F2.wireOp",EDGE,"E90.MirrorCS");Q131=makeQuery(id+"F2.imprint","IMPRINT",FACE,{"disambiguationData":[TD([[makeQuery(id+"F2.imprint","IMPRINT",EDGE,{"derivedFrom":subQ0}),1.0]])]});}
            var Q132;
            {var subQ0=sQuery(id+"F2.wireOp",EDGE,"E71.MirrorCS");Q132=makeQuery(id+"F2.imprint","IMPRINT",FACE,{"disambiguationData":[TD([[makeQuery(id+"F2.imprint","IMPRINT",EDGE,{"derivedFrom":subQ0}),1.0]])]});}
            var Q133;
            {var subQ0=sQuery(id+"F2.wireOp",EDGE,"E11.MirrorCS");Q133=makeQuery(id+"F2.imprint","IMPRINT",FACE,{"disambiguationData":[TD([[makeQuery(id+"F2.imprint","IMPRINT",EDGE,{"derivedFrom":subQ0}),-1.0]])]});}
            var Q134;
            {var subQ0=sQuery(id+"F2.wireOp",EDGE,"E10.5.0.1");var subQ1=sQuery(id+"F2.wireOp",EDGE,"E9.bottom");var subQ2=makeQuery(id+"F2.imprint","INTERSECT",VERTEX,{"derivedFrom":[subQ1,subQ0]});Q134=makeQuery(id+"F2.imprint","IMPRINT",FACE,{"disambiguationData":[TD([[makeQuery(id+"F2.imprint","IMPRINT",EDGE,{"disambiguationData":[TD([[subQ2,-1.0]])],"derivedFrom":subQ1}),-1.0]])]});}
            var Q135;
            {var subQ0=sQuery(id+"F2.wireOp",EDGE,"E133.MirrorCS");Q135=makeQuery(id+"F2.imprint","IMPRINT",FACE,{"disambiguationData":[TD([[makeQuery(id+"F2.imprint","IMPRINT",EDGE,{"derivedFrom":subQ0}),-1.0]])]});}
            var Q136;
            {var subQ0=sQuery(id+"F2.wireOp",EDGE,"E10.9.0.0");var subQ1=sQuery(id+"F2.wireOp",EDGE,"E9.bottom");var subQ2=makeQuery(id+"F2.imprint","INTERSECT",VERTEX,{"derivedFrom":[subQ1,subQ0]});Q136=makeQuery(id+"F2.imprint","IMPRINT",FACE,{"disambiguationData":[TD([[makeQuery(id+"F2.imprint","IMPRINT",EDGE,{"disambiguationData":[TD([[subQ2,-1.0]])],"derivedFrom":subQ1}),-1.0]])]});}
            var Q137;
            {var subQ0=sQuery(id+"F2.wireOp",EDGE,"E161.MirrorCS");var subQ1=sQuery(id+"F2.wireOp",EDGE,"E149.MirrorCS");var subQ2=makeQuery(id+"F2.imprint","INTERSECT",VERTEX,{"derivedFrom":[subQ1,subQ0]});Q137=makeQuery(id+"F2.imprint","IMPRINT",FACE,{"disambiguationData":[TD([[makeQuery(id+"F2.imprint","IMPRINT",EDGE,{"disambiguationData":[TD([[subQ2,-1.0]])],"derivedFrom":subQ1}),1.0]])]});}
            var Q138;
            {var subQ5=sQuery(id+"F2.wireOp",EDGE,"E10.1.0.3");Q138=makeQuery(id+"F2.imprint","IMPRINT",FACE,{"disambiguationData":[TD([[makeQuery(id+"F2.imprint","IMPRINT",EDGE,{"derivedFrom":subQ5}),1.0]])]});}
            var Q139;
            {var subQ5=sQuery(id+"F2.wireOp",EDGE,"E10.1.0.2");Q139=makeQuery(id+"F2.imprint","IMPRINT",FACE,{"disambiguationData":[TD([[makeQuery(id+"F2.imprint","IMPRINT",EDGE,{"derivedFrom":subQ5}),-1.0]])]});}
            var Q140;
            {var subQ5=sQuery(id+"F2.wireOp",EDGE,"E10.4.0.2");Q140=makeQuery(id+"F2.imprint","IMPRINT",FACE,{"disambiguationData":[TD([[makeQuery(id+"F2.imprint","IMPRINT",EDGE,{"derivedFrom":subQ5}),-1.0]])]});}
            var Q141;
            {var subQ5=sQuery(id+"F2.wireOp",EDGE,"E10.5.0.2");Q141=makeQuery(id+"F2.imprint","IMPRINT",FACE,{"disambiguationData":[TD([[makeQuery(id+"F2.imprint","IMPRINT",EDGE,{"derivedFrom":subQ5}),-1.0]])]});}
            var Q142;
            {var subQ5=sQuery(id+"F2.wireOp",EDGE,"E10.8.0.2");Q142=makeQuery(id+"F2.imprint","IMPRINT",FACE,{"disambiguationData":[TD([[makeQuery(id+"F2.imprint","IMPRINT",EDGE,{"derivedFrom":subQ5}),-1.0]])]});}
            var Q143;
            {var subQ5=sQuery(id+"F2.wireOp",EDGE,"E10.11.0.2");Q143=makeQuery(id+"F2.imprint","IMPRINT",FACE,{"disambiguationData":[TD([[makeQuery(id+"F2.imprint","IMPRINT",EDGE,{"derivedFrom":subQ5}),-1.0]])]});}
            var Q144;
            {var subQ0=sQuery(id+"F2.wireOp",EDGE,"E72.MirrorCS");Q144=makeQuery(id+"F2.imprint","IMPRINT",FACE,{"disambiguationData":[TD([[makeQuery(id+"F2.imprint","IMPRINT",EDGE,{"derivedFrom":subQ0}),-1.0]])]});}
            var Q145;
            {var subQ0=sQuery(id+"F2.wireOp",EDGE,"E111.MirrorCS");var subQ1=sQuery(id+"F2.wireOp",EDGE,"E88.MirrorCS");var subQ2=makeQuery(id+"F2.imprint","INTERSECT",VERTEX,{"derivedFrom":[subQ1,subQ0]});Q145=makeQuery(id+"F2.imprint","IMPRINT",FACE,{"disambiguationData":[TD([[makeQuery(id+"F2.imprint","IMPRINT",EDGE,{"disambiguationData":[TD([[subQ2,-1.0]])],"derivedFrom":subQ1}),1.0]])]});}
            var Q146;
            {var subQ0=sQuery(id+"F2.wireOp",EDGE,"E10.6.0.1");var subQ1=sQuery(id+"F2.wireOp",EDGE,"E9.bottom");var subQ2=makeQuery(id+"F2.imprint","INTERSECT",VERTEX,{"derivedFrom":[subQ1,subQ0]});Q146=makeQuery(id+"F2.imprint","IMPRINT",FACE,{"disambiguationData":[TD([[makeQuery(id+"F2.imprint","IMPRINT",EDGE,{"disambiguationData":[TD([[subQ2,-1.0]])],"derivedFrom":subQ1}),-1.0]])]});}
            var Q147;
            {var subQ0=sQuery(id+"F2.wireOp",EDGE,"E111.MirrorCS");var subQ1=sQuery(id+"F2.wireOp",EDGE,"E94.MirrorCS");var subQ2=makeQuery(id+"F2.imprint","INTERSECT",VERTEX,{"derivedFrom":[subQ1,subQ0]});Q147=makeQuery(id+"F2.imprint","IMPRINT",FACE,{"disambiguationData":[TD([[makeQuery(id+"F2.imprint","IMPRINT",EDGE,{"disambiguationData":[TD([[subQ2,-1.0]])],"derivedFrom":subQ1}),1.0]])]});}
            var Q148;
            {var subQ0=sQuery(id+"F2.wireOp",EDGE,"E10.10.0.0");var subQ1=sQuery(id+"F2.wireOp",EDGE,"E9.bottom");var subQ2=makeQuery(id+"F2.imprint","INTERSECT",VERTEX,{"derivedFrom":[subQ1,subQ0]});Q148=makeQuery(id+"F2.imprint","IMPRINT",FACE,{"disambiguationData":[TD([[makeQuery(id+"F2.imprint","IMPRINT",EDGE,{"disambiguationData":[TD([[subQ2,-1.0]])],"derivedFrom":subQ1}),-1.0]])]});}
            var Q149;
            {var subQ0=sQuery(id+"F2.wireOp",EDGE,"E161.MirrorCS");var subQ1=sQuery(id+"F2.wireOp",EDGE,"E150.MirrorCS");var subQ2=makeQuery(id+"F2.imprint","INTERSECT",VERTEX,{"derivedFrom":[subQ1,subQ0]});Q149=makeQuery(id+"F2.imprint","IMPRINT",FACE,{"disambiguationData":[TD([[makeQuery(id+"F2.imprint","IMPRINT",EDGE,{"disambiguationData":[TD([[subQ2,-1.0]])],"derivedFrom":subQ1}),1.0]])]});}
            var Q150;
            {var subQ0=sQuery(id+"F2.wireOp",EDGE,"E111.MirrorCS");var subQ1=sQuery(id+"F2.wireOp",EDGE,"E89.MirrorCS");var subQ2=makeQuery(id+"F2.imprint","INTERSECT",VERTEX,{"derivedFrom":[subQ1,subQ0]});Q150=makeQuery(id+"F2.imprint","IMPRINT",FACE,{"disambiguationData":[TD([[makeQuery(id+"F2.imprint","IMPRINT",EDGE,{"disambiguationData":[TD([[subQ2,-1.0]])],"derivedFrom":subQ1}),-1.0]])]});}
            var Q151;
            {var subQ0=sQuery(id+"F2.wireOp",EDGE,"E10.7.0.1");var subQ1=sQuery(id+"F2.wireOp",EDGE,"E9.bottom");var subQ2=makeQuery(id+"F2.imprint","INTERSECT",VERTEX,{"derivedFrom":[subQ1,subQ0]});Q151=makeQuery(id+"F2.imprint","IMPRINT",FACE,{"disambiguationData":[TD([[makeQuery(id+"F2.imprint","IMPRINT",EDGE,{"disambiguationData":[TD([[subQ2,-1.0]])],"derivedFrom":subQ1}),-1.0]])]});}
            var Q152;
            {var subQ0=sQuery(id+"F2.wireOp",EDGE,"E117.MirrorCS");Q152=makeQuery(id+"F2.imprint","IMPRINT",FACE,{"disambiguationData":[TD([[makeQuery(id+"F2.imprint","IMPRINT",EDGE,{"derivedFrom":subQ0}),-1.0]])]});}
            var Q153;
            {var subQ0=sQuery(id+"F2.wireOp",EDGE,"E161.MirrorCS");var subQ1=sQuery(id+"F2.wireOp",EDGE,"E151.MirrorCS");var subQ2=makeQuery(id+"F2.imprint","INTERSECT",VERTEX,{"derivedFrom":[subQ1,subQ0]});Q153=makeQuery(id+"F2.imprint","IMPRINT",FACE,{"disambiguationData":[TD([[makeQuery(id+"F2.imprint","IMPRINT",EDGE,{"disambiguationData":[TD([[subQ2,-1.0]])],"derivedFrom":subQ1}),1.0]])]});}
            var Q154;
            {var subQ0=sQuery(id+"F2.wireOp",EDGE,"E111.MirrorCS");var subQ1=sQuery(id+"F2.wireOp",EDGE,"E95.MirrorCS");var subQ2=makeQuery(id+"F2.imprint","INTERSECT",VERTEX,{"derivedFrom":[subQ1,subQ0]});Q154=makeQuery(id+"F2.imprint","IMPRINT",FACE,{"disambiguationData":[TD([[makeQuery(id+"F2.imprint","IMPRINT",EDGE,{"disambiguationData":[TD([[subQ2,-1.0]])],"derivedFrom":subQ1}),-1.0]])]});}
            var Q155;
            {var subQ0=sQuery(id+"F2.wireOp",EDGE,"E161.MirrorCS");var subQ1=sQuery(id+"F2.wireOp",EDGE,"E151.MirrorCS");var subQ2=makeQuery(id+"F2.imprint","INTERSECT",VERTEX,{"derivedFrom":[subQ1,subQ0]});Q155=makeQuery(id+"F2.imprint","IMPRINT",FACE,{"disambiguationData":[TD([[makeQuery(id+"F2.imprint","IMPRINT",EDGE,{"disambiguationData":[TD([[subQ2,-1.0]])],"derivedFrom":subQ1}),-1.0]])]});}
            var Q156;
            {var subQ0=sQuery(id+"F2.wireOp",EDGE,"E59.MirrorCS");var subQ1=sQuery(id+"F2.wireOp",EDGE,"E41.MirrorCS");var subQ2=makeQuery(id+"F2.imprint","INTERSECT",VERTEX,{"derivedFrom":[subQ1,subQ0]});Q156=makeQuery(id+"F2.imprint","IMPRINT",FACE,{"disambiguationData":[TD([[makeQuery(id+"F2.imprint","IMPRINT",EDGE,{"disambiguationData":[TD([[subQ2,-1.0]])],"derivedFrom":subQ1}),1.0]])]});}
            var Q157;
            {var subQ0=sQuery(id+"F2.wireOp",EDGE,"E62.MirrorCS");var subQ1=sQuery(id+"F2.wireOp",EDGE,"E41.MirrorCS");var subQ2=makeQuery(id+"F2.imprint","INTERSECT",VERTEX,{"derivedFrom":[subQ1,subQ0]});Q157=makeQuery(id+"F2.imprint","IMPRINT",FACE,{"disambiguationData":[TD([[makeQuery(id+"F2.imprint","IMPRINT",EDGE,{"disambiguationData":[TD([[subQ2,-1.0]])],"derivedFrom":subQ1}),1.0]])]});}
            var Q158;
            {var subQ0=sQuery(id+"F2.wireOp",EDGE,"E157.MirrorCS");var subQ1=sQuery(id+"F2.wireOp",EDGE,"E156.MirrorCS");var subQ2=makeQuery(id+"F2.imprint","INTERSECT",VERTEX,{"derivedFrom":[subQ1,subQ0]});Q158=makeQuery(id+"F2.imprint","IMPRINT",FACE,{"disambiguationData":[TD([[makeQuery(id+"F2.imprint","IMPRINT",EDGE,{"disambiguationData":[TD([[subQ2,-1.0]])],"derivedFrom":subQ1}),-1.0]])]});}
            var Q159;
            {var subQ0=sQuery(id+"F2.wireOp",EDGE,"E49.MirrorCS");var subQ1=sQuery(id+"F2.wireOp",EDGE,"E41.MirrorCS");var subQ2=makeQuery(id+"F2.imprint","INTERSECT",VERTEX,{"derivedFrom":[subQ1,subQ0]});Q159=makeQuery(id+"F2.imprint","IMPRINT",FACE,{"disambiguationData":[TD([[makeQuery(id+"F2.imprint","IMPRINT",EDGE,{"disambiguationData":[TD([[subQ2,-1.0]])],"derivedFrom":subQ1}),1.0]])]});}
            var Q160;
            {var subQ0=sQuery(id+"F2.wireOp",EDGE,"E41.MirrorCS");var subQ1=sQuery(id+"F2.wireOp",EDGE,"E38.MirrorCS");var subQ2=makeQuery(id+"F2.imprint","INTERSECT",VERTEX,{"derivedFrom":[subQ1,subQ0]});Q160=makeQuery(id+"F2.imprint","IMPRINT",FACE,{"disambiguationData":[TD([[makeQuery(id+"F2.imprint","IMPRINT",EDGE,{"disambiguationData":[TD([[subQ2,-1.0]])],"derivedFrom":subQ1}),1.0]])]});}
            var Q161;
            {var subQ0=sQuery(id+"F2.wireOp",EDGE,"E58.MirrorCS");var subQ1=sQuery(id+"F2.wireOp",EDGE,"E41.MirrorCS");var subQ2=makeQuery(id+"F2.imprint","INTERSECT",VERTEX,{"derivedFrom":[subQ1,subQ0]});Q161=makeQuery(id+"F2.imprint","IMPRINT",FACE,{"disambiguationData":[TD([[makeQuery(id+"F2.imprint","IMPRINT",EDGE,{"disambiguationData":[TD([[subQ2,-1.0]])],"derivedFrom":subQ1}),1.0]])]});}
            var Q162;
            {var subQ5=sQuery(id+"F2.wireOp",EDGE,"E9.left");Q162=makeQuery(id+"F2.imprint","IMPRINT",FACE,{"disambiguationData":[TD([[makeQuery(id+"F2.imprint","IMPRINT",EDGE,{"derivedFrom":subQ5}),1.0]])]});}
            var Q163;
            {var subQ0=sQuery(id+"F2.wireOp",EDGE,"E53.MirrorCS");var subQ1=sQuery(id+"F2.wireOp",EDGE,"E41.MirrorCS");var subQ2=makeQuery(id+"F2.imprint","INTERSECT",VERTEX,{"derivedFrom":[subQ1,subQ0]});Q163=makeQuery(id+"F2.imprint","IMPRINT",FACE,{"disambiguationData":[TD([[makeQuery(id+"F2.imprint","IMPRINT",EDGE,{"disambiguationData":[TD([[subQ2,-1.0]])],"derivedFrom":subQ1}),1.0]])]});}
            var Q164;
            {var subQ5=sQuery(id+"F2.wireOp",EDGE,"E136.MirrorCS");Q164=makeQuery(id+"F2.imprint","IMPRINT",FACE,{"disambiguationData":[TD([[makeQuery(id+"F2.imprint","IMPRINT",EDGE,{"derivedFrom":subQ5}),1.0]])]});}
            var Q165;
            {var subQ0=sQuery(id+"F2.wireOp",EDGE,"E41.MirrorCS");var subQ1=sQuery(id+"F2.wireOp",EDGE,"E21.MirrorCS");var subQ2=makeQuery(id+"F2.imprint","INTERSECT",VERTEX,{"derivedFrom":[subQ1,subQ0]});Q165=makeQuery(id+"F2.imprint","IMPRINT",FACE,{"disambiguationData":[TD([[makeQuery(id+"F2.imprint","IMPRINT",EDGE,{"disambiguationData":[TD([[subQ2,-1.0]])],"derivedFrom":subQ1}),1.0]])]});}
            var Q166;
            {var subQ0=sQuery(id+"F2.wireOp",EDGE,"E42.MirrorCS");var subQ1=sQuery(id+"F2.wireOp",EDGE,"E41.MirrorCS");var subQ2=makeQuery(id+"F2.imprint","INTERSECT",VERTEX,{"derivedFrom":[subQ1,subQ0]});Q166=makeQuery(id+"F2.imprint","IMPRINT",FACE,{"disambiguationData":[TD([[makeQuery(id+"F2.imprint","IMPRINT",EDGE,{"disambiguationData":[TD([[subQ2,-1.0]])],"derivedFrom":subQ1}),1.0]])]});}
            var Q167;
            {var subQ0=sQuery(id+"F2.wireOp",EDGE,"E57.MirrorCS");var subQ1=sQuery(id+"F2.wireOp",EDGE,"E41.MirrorCS");var subQ2=makeQuery(id+"F2.imprint","INTERSECT",VERTEX,{"derivedFrom":[subQ1,subQ0]});Q167=makeQuery(id+"F2.imprint","IMPRINT",FACE,{"disambiguationData":[TD([[makeQuery(id+"F2.imprint","IMPRINT",EDGE,{"disambiguationData":[TD([[subQ2,-1.0]])],"derivedFrom":subQ1}),1.0]])]});}
            var Q168;
            {var subQ0=sQuery(id+"F2.wireOp",EDGE,"E161.MirrorCS");var subQ1=sQuery(id+"F2.wireOp",EDGE,"E123.MirrorCS");var subQ2=makeQuery(id+"F2.imprint","INTERSECT",VERTEX,{"derivedFrom":[subQ1,subQ0]});Q168=makeQuery(id+"F2.imprint","IMPRINT",FACE,{"disambiguationData":[TD([[makeQuery(id+"F2.imprint","IMPRINT",EDGE,{"disambiguationData":[TD([[subQ2,-1.0]])],"derivedFrom":subQ1}),1.0]])]});}
            var Q169;
            {var subQ0=sQuery(id+"F2.wireOp",EDGE,"E41.MirrorCS");var subQ1=sQuery(id+"F2.wireOp",EDGE,"E27.MirrorCS");var subQ2=makeQuery(id+"F2.imprint","INTERSECT",VERTEX,{"derivedFrom":[subQ1,subQ0]});Q169=makeQuery(id+"F2.imprint","IMPRINT",FACE,{"disambiguationData":[TD([[makeQuery(id+"F2.imprint","IMPRINT",EDGE,{"disambiguationData":[TD([[subQ2,-1.0]])],"derivedFrom":subQ1}),1.0]])]});}
            var Q170;
            {var subQ0=sQuery(id+"F2.wireOp",EDGE,"E47.MirrorCS");var subQ1=sQuery(id+"F2.wireOp",EDGE,"E41.MirrorCS");var subQ2=makeQuery(id+"F2.imprint","INTERSECT",VERTEX,{"derivedFrom":[subQ1,subQ0]});Q170=makeQuery(id+"F2.imprint","IMPRINT",FACE,{"disambiguationData":[TD([[makeQuery(id+"F2.imprint","IMPRINT",EDGE,{"disambiguationData":[TD([[subQ2,-1.0]])],"derivedFrom":subQ1}),1.0]])]});}
            var Q171;
            {var subQ0=sQuery(id+"F2.wireOp",EDGE,"E41.MirrorCS");var subQ1=sQuery(id+"F2.wireOp",EDGE,"E21.MirrorCS");var subQ2=makeQuery(id+"F2.imprint","INTERSECT",VERTEX,{"derivedFrom":[subQ1,subQ0]});Q171=makeQuery(id+"F2.imprint","IMPRINT",FACE,{"disambiguationData":[TD([[makeQuery(id+"F2.imprint","IMPRINT",EDGE,{"disambiguationData":[TD([[subQ2,-1.0]])],"derivedFrom":subQ1}),-1.0]])]});}
            var Q172;
            {var subQ0=sQuery(id+"F2.wireOp",EDGE,"E44.MirrorCS");var subQ1=sQuery(id+"F2.wireOp",EDGE,"E41.MirrorCS");var subQ2=makeQuery(id+"F2.imprint","INTERSECT",VERTEX,{"derivedFrom":[subQ1,subQ0]});Q172=makeQuery(id+"F2.imprint","IMPRINT",FACE,{"disambiguationData":[TD([[makeQuery(id+"F2.imprint","IMPRINT",EDGE,{"disambiguationData":[TD([[subQ2,-1.0]])],"derivedFrom":subQ1}),1.0]])]});}
            var Q173;
            {var subQ0=sQuery(id+"F2.wireOp",EDGE,"E43.MirrorCS");var subQ1=sQuery(id+"F2.wireOp",EDGE,"E41.MirrorCS");var subQ2=makeQuery(id+"F2.imprint","INTERSECT",VERTEX,{"derivedFrom":[subQ1,subQ0]});Q173=makeQuery(id+"F2.imprint","IMPRINT",FACE,{"disambiguationData":[TD([[makeQuery(id+"F2.imprint","IMPRINT",EDGE,{"disambiguationData":[TD([[subQ2,-1.0]])],"derivedFrom":subQ1}),1.0]])]});}
            var Q174;
            {var subQ0=sQuery(id+"F2.wireOp",EDGE,"E60.MirrorCS");var subQ1=sQuery(id+"F2.wireOp",EDGE,"E41.MirrorCS");var subQ2=makeQuery(id+"F2.imprint","INTERSECT",VERTEX,{"derivedFrom":[subQ1,subQ0]});Q174=makeQuery(id+"F2.imprint","IMPRINT",FACE,{"disambiguationData":[TD([[makeQuery(id+"F2.imprint","IMPRINT",EDGE,{"disambiguationData":[TD([[subQ2,-1.0]])],"derivedFrom":subQ1}),1.0]])]});}
            var Q175;
            {var subQ0=sQuery(id+"F2.wireOp",EDGE,"E56.MirrorCS");var subQ1=sQuery(id+"F2.wireOp",EDGE,"E41.MirrorCS");var subQ2=makeQuery(id+"F2.imprint","INTERSECT",VERTEX,{"derivedFrom":[subQ1,subQ0]});Q175=makeQuery(id+"F2.imprint","IMPRINT",FACE,{"disambiguationData":[TD([[makeQuery(id+"F2.imprint","IMPRINT",EDGE,{"disambiguationData":[TD([[subQ2,-1.0]])],"derivedFrom":subQ1}),1.0]])]});}
            var Q176;
            {var subQ0=sQuery(id+"F2.wireOp",EDGE,"E156.MirrorCS");var subQ1=sQuery(id+"F2.wireOp",EDGE,"E124.MirrorCS");var subQ2=makeQuery(id+"F2.imprint","INTERSECT",VERTEX,{"derivedFrom":[subQ1,subQ0]});Q176=makeQuery(id+"F2.imprint","IMPRINT",FACE,{"disambiguationData":[TD([[makeQuery(id+"F2.imprint","IMPRINT",EDGE,{"disambiguationData":[TD([[subQ2,1.0]])],"derivedFrom":subQ1}),-1.0]])]});}
            var Q177;
            {var subQ0=sQuery(id+"F2.wireOp",EDGE,"E61.MirrorCS");var subQ1=sQuery(id+"F2.wireOp",EDGE,"E41.MirrorCS");var subQ2=makeQuery(id+"F2.imprint","INTERSECT",VERTEX,{"derivedFrom":[subQ1,subQ0]});Q177=makeQuery(id+"F2.imprint","IMPRINT",FACE,{"disambiguationData":[TD([[makeQuery(id+"F2.imprint","IMPRINT",EDGE,{"disambiguationData":[TD([[subQ2,-1.0]])],"derivedFrom":subQ1}),1.0]])]});}
            var Q178;
            {var subQ0=sQuery(id+"F2.wireOp",EDGE,"E63.MirrorCS");var subQ1=sQuery(id+"F2.wireOp",EDGE,"E41.MirrorCS");var subQ2=makeQuery(id+"F2.imprint","INTERSECT",VERTEX,{"derivedFrom":[subQ1,subQ0]});Q178=makeQuery(id+"F2.imprint","IMPRINT",FACE,{"disambiguationData":[TD([[makeQuery(id+"F2.imprint","IMPRINT",EDGE,{"disambiguationData":[TD([[subQ2,-1.0]])],"derivedFrom":subQ1}),1.0]])]});}
            var Q179;
            {var subQ0=sQuery(id+"F2.wireOp",EDGE,"E54.MirrorCS");var subQ1=sQuery(id+"F2.wireOp",EDGE,"E41.MirrorCS");var subQ2=makeQuery(id+"F2.imprint","INTERSECT",VERTEX,{"derivedFrom":[subQ1,subQ0]});Q179=makeQuery(id+"F2.imprint","IMPRINT",FACE,{"disambiguationData":[TD([[makeQuery(id+"F2.imprint","IMPRINT",EDGE,{"disambiguationData":[TD([[subQ2,-1.0]])],"derivedFrom":subQ1}),1.0]])]});}
            var Q180;
            {var subQ0=sQuery(id+"F2.wireOp",EDGE,"E46.MirrorCS");var subQ1=sQuery(id+"F2.wireOp",EDGE,"E41.MirrorCS");var subQ2=makeQuery(id+"F2.imprint","INTERSECT",VERTEX,{"derivedFrom":[subQ1,subQ0]});Q180=makeQuery(id+"F2.imprint","IMPRINT",FACE,{"disambiguationData":[TD([[makeQuery(id+"F2.imprint","IMPRINT",EDGE,{"disambiguationData":[TD([[subQ2,-1.0]])],"derivedFrom":subQ1}),1.0]])]});}
            var Q181;
            {var subQ0=sQuery(id+"F2.wireOp",EDGE,"E48.MirrorCS");var subQ1=sQuery(id+"F2.wireOp",EDGE,"E41.MirrorCS");var subQ2=makeQuery(id+"F2.imprint","INTERSECT",VERTEX,{"derivedFrom":[subQ1,subQ0]});Q181=makeQuery(id+"F2.imprint","IMPRINT",FACE,{"disambiguationData":[TD([[makeQuery(id+"F2.imprint","IMPRINT",EDGE,{"disambiguationData":[TD([[subQ2,-1.0]])],"derivedFrom":subQ1}),1.0]])]});}
            var Q182;
            {var subQ0=sQuery(id+"F2.wireOp",EDGE,"E45.MirrorCS");var subQ1=sQuery(id+"F2.wireOp",EDGE,"E41.MirrorCS");var subQ2=makeQuery(id+"F2.imprint","INTERSECT",VERTEX,{"derivedFrom":[subQ1,subQ0]});Q182=makeQuery(id+"F2.imprint","IMPRINT",FACE,{"disambiguationData":[TD([[makeQuery(id+"F2.imprint","IMPRINT",EDGE,{"disambiguationData":[TD([[subQ2,-1.0]])],"derivedFrom":subQ1}),1.0]])]});}
            var Q183;
            {var subQ0=sQuery(id+"F2.wireOp",EDGE,"E51.MirrorCS");var subQ1=sQuery(id+"F2.wireOp",EDGE,"E41.MirrorCS");var subQ2=makeQuery(id+"F2.imprint","INTERSECT",VERTEX,{"derivedFrom":[subQ1,subQ0]});Q183=makeQuery(id+"F2.imprint","IMPRINT",FACE,{"disambiguationData":[TD([[makeQuery(id+"F2.imprint","IMPRINT",EDGE,{"disambiguationData":[TD([[subQ2,-1.0]])],"derivedFrom":subQ1}),1.0]])]});}
            var Q184;
            {var subQ0=sQuery(id+"F2.wireOp",EDGE,"E161.MirrorCS");var subQ1=sQuery(id+"F2.wireOp",EDGE,"E149.MirrorCS");var subQ2=makeQuery(id+"F2.imprint","INTERSECT",VERTEX,{"derivedFrom":[subQ1,subQ0]});Q184=makeQuery(id+"F2.imprint","IMPRINT",FACE,{"disambiguationData":[TD([[makeQuery(id+"F2.imprint","IMPRINT",EDGE,{"disambiguationData":[TD([[subQ2,-1.0]])],"derivedFrom":subQ1}),-1.0]])]});}
            var Q185;
            {var subQ0=sQuery(id+"F2.wireOp",EDGE,"E111.MirrorCS");var subQ1=sQuery(id+"F2.wireOp",EDGE,"E89.MirrorCS");var subQ2=makeQuery(id+"F2.imprint","INTERSECT",VERTEX,{"derivedFrom":[subQ1,subQ0]});Q185=makeQuery(id+"F2.imprint","IMPRINT",FACE,{"disambiguationData":[TD([[makeQuery(id+"F2.imprint","IMPRINT",EDGE,{"disambiguationData":[TD([[subQ2,-1.0]])],"derivedFrom":subQ1}),1.0]])]});}
            var Q186;
            {var subQ0=sQuery(id+"F2.wireOp",EDGE,"E9.right");Q186=makeQuery(id+"F2.imprint","IMPRINT",FACE,{"disambiguationData":[TD([[makeQuery(id+"F2.imprint","IMPRINT",EDGE,{"derivedFrom":subQ0}),-1.0]])]});}
            var Q187;
            {var subQ0=sQuery(id+"F2.wireOp",EDGE,"E161.MirrorCS");var subQ1=sQuery(id+"F2.wireOp",EDGE,"E150.MirrorCS");var subQ2=makeQuery(id+"F2.imprint","INTERSECT",VERTEX,{"derivedFrom":[subQ1,subQ0]});Q187=makeQuery(id+"F2.imprint","IMPRINT",FACE,{"disambiguationData":[TD([[makeQuery(id+"F2.imprint","IMPRINT",EDGE,{"disambiguationData":[TD([[subQ2,-1.0]])],"derivedFrom":subQ1}),-1.0]])]});}
            var Q188;
            {var subQ0=sQuery(id+"F2.wireOp",EDGE,"E10.11.0.0");var subQ1=sQuery(id+"F2.wireOp",EDGE,"E9.bottom");var subQ2=makeQuery(id+"F2.imprint","INTERSECT",VERTEX,{"derivedFrom":[subQ1,subQ0]});Q188=makeQuery(id+"F2.imprint","IMPRINT",FACE,{"disambiguationData":[TD([[makeQuery(id+"F2.imprint","IMPRINT",EDGE,{"disambiguationData":[TD([[subQ2,-1.0]])],"derivedFrom":subQ1}),-1.0]])]});}
            var Q189;
            {var subQ0=sQuery(id+"F2.wireOp",EDGE,"E13.MirrorCS");Q189=makeQuery(id+"F2.imprint","IMPRINT",FACE,{"disambiguationData":[TD([[makeQuery(id+"F2.imprint","IMPRINT",EDGE,{"derivedFrom":subQ0}),1.0]])]});}
            var Q190;
            {var subQ0=sQuery(id+"F2.wireOp",EDGE,"E85.MirrorCS");Q190=makeQuery(id+"F2.imprint","IMPRINT",FACE,{"disambiguationData":[TD([[makeQuery(id+"F2.imprint","IMPRINT",EDGE,{"derivedFrom":subQ0}),-1.0]])]});}
            var Q191;
            {var subQ0=sQuery(id+"F2.wireOp",EDGE,"E84.MirrorCS");Q191=makeQuery(id+"F2.imprint","IMPRINT",FACE,{"disambiguationData":[TD([[makeQuery(id+"F2.imprint","IMPRINT",EDGE,{"derivedFrom":subQ0}),1.0]])]});}
            extrude(context, id + "F3", {"entities" : qUnion([Q0, Q1, Q2, Q3, Q4, Q5, Q6, Q7, Q8, Q9, Q10, Q11, Q12, Q13, Q14, Q15, Q16, Q17, Q18, Q19, Q20, Q21, Q22, Q23, Q24, Q25, Q26, Q27, Q28, Q29, Q30, Q31, Q32, Q33, Q34, Q35, Q36, Q37, Q38, Q39, Q40, Q41, Q42, Q43, Q44, Q45, Q46, Q47, Q48, Q49, Q50, Q51, Q52, Q53, Q54, Q55, Q56, Q57, Q58, Q59, Q60, Q61, Q62, Q63, Q64, Q65, Q66, Q67, Q68, Q69, Q70, Q71, Q72, Q73, Q74, Q75, Q76, Q77, Q78, Q79, Q80, Q81, Q82, Q83, Q84, Q85, Q86, Q87, Q88, Q89, Q90, Q91, Q92, Q93, Q94, Q95, Q96, Q97, Q98, Q99, Q100, Q101, Q102, Q103, Q104, Q105, Q106, Q107, Q108, Q109, Q110, Q111, Q112, Q113, Q114, Q115, Q116, Q117, Q118, Q119, Q120, Q121, Q122, Q123, Q124, Q125, Q126, Q127, Q128, Q129, Q130, Q131, Q132, Q133, Q134, Q135, Q136, Q137, Q138, Q139, Q140, Q141, Q142, Q143, Q144, Q145, Q146, Q147, Q148, Q149, Q150, Q151, Q152, Q153, Q154, Q155, Q156, Q157, Q158, Q159, Q160, Q161, Q162, Q163, Q164, Q165, Q166, Q167, Q168, Q169, Q170, Q171, Q172, Q173, Q174, Q175, Q176, Q177, Q178, Q179, Q180, Q181, Q182, Q183, Q184, Q185, Q186, Q187, Q188, Q189, Q190, Q191]), "operationType" : NewBodyOperationType.ADD, "depth" : 7.62 * mm});
        }
        {
            var Q0;
            Q0=qCreatedBy(makeId("Front.planeOp"),FACE);
            var sketch = newSketch(context, id + "F4", { "sketchPlane" : qUnion([Q0])});
            skText(sketch, "E170", { "text": "REFLECTIVE", "fontName": "OpenSans-BoldItalic.ttf"});
            skText(sketch, "E171", { "text": "INTUITIVE", "fontName": "OpenSans-BoldItalic.ttf"});
            skText(sketch, "E172", { "text": "VERBAL", "fontName": "OpenSans-BoldItalic.ttf"});
            skText(sketch, "E173", { "text": "GLOBAL", "fontName": "OpenSans-BoldItalic.ttf"});
            const initialGuessF4  = {"E170": [0.14562, 0.02874, 1, 0, 0.00947], "E171": [0.1523, 0.00148, 1, 0, 0.00947], "E172": [0.15175, -0.02831, 1, 0, 0.00947], "E173": [0.15202, -0.06064, 1, 0, 0.00947]};
            skSetInitialGuess(sketch, initialGuessF4);
            skSolve(sketch);
        }
        {
            var Q0;
            Q0 = qSketchRegion(id + "F4", true);
            extrude(context, id + "F5", {"entities" : qUnion([Q0]), "operationType" : NewBodyOperationType.ADD, "depth" : 7.62 * mm});
        }
        {
            var Q0;
            Q0=qCreatedBy(makeId("Front.planeOp"),FACE);
            var sketch = newSketch(context, id + "F6", { "sketchPlane" : qUnion([Q0])});
            skText(sketch, "E174", { "text": "11 9 7 5 3 1 1 3 5 7 9 11", "fontName": "OpenSans-BoldItalic.ttf"});
            const initialGuessF6  = {"E174": [-0.01678, 0.01704, 1, 0, 0.00947]};
            skSetInitialGuess(sketch, initialGuessF6);
            skSolve(sketch);
        }
        {
            var Q0;
            Q0 = qSketchRegion(id + "F6", true);
            extrude(context, id + "F7", {"entities" : qUnion([Q0]), "depth" : 7.62 * mm});
        }
        {
            var Q0;
            Q0=qCreatedBy(makeId("Front.planeOp"),FACE);
            var sketch = newSketch(context, id + "F8", { "sketchPlane" : qUnion([Q0])});
            skText(sketch, "E175", { "text": "11 9 7 5 3 1 1 3 5 7 9 11", "fontName": "OpenSans-BoldItalic.ttf"});
            skText(sketch, "E176", { "text": "11 9 7 5 3 1 1 3 5 7 9 11", "fontName": "OpenSans-BoldItalic.ttf"});
            skText(sketch, "E177", { "text": "11 9 7 5 3 1 1 3 5 7 9 11", "fontName": "OpenSans-BoldItalic.ttf"});
            const initialGuessF8  = {"E175": [-0.01625, -0.04343, 1, 0, 0.00947], "E176": [-0.01677, -0.01356, 1, 0, 0.00947], "E177": [-0.017, -0.0713, 1, 0, 0.00947]};
            skSetInitialGuess(sketch, initialGuessF8);
            skSolve(sketch);
        }
        {
            var Q0;
            Q0 = qSketchRegion(id + "F8", true);
            extrude(context, id + "F9", {"entities" : qUnion([Q0]), "operationType" : NewBodyOperationType.ADD, "depth" : 7.62 * mm});
        }
    });
